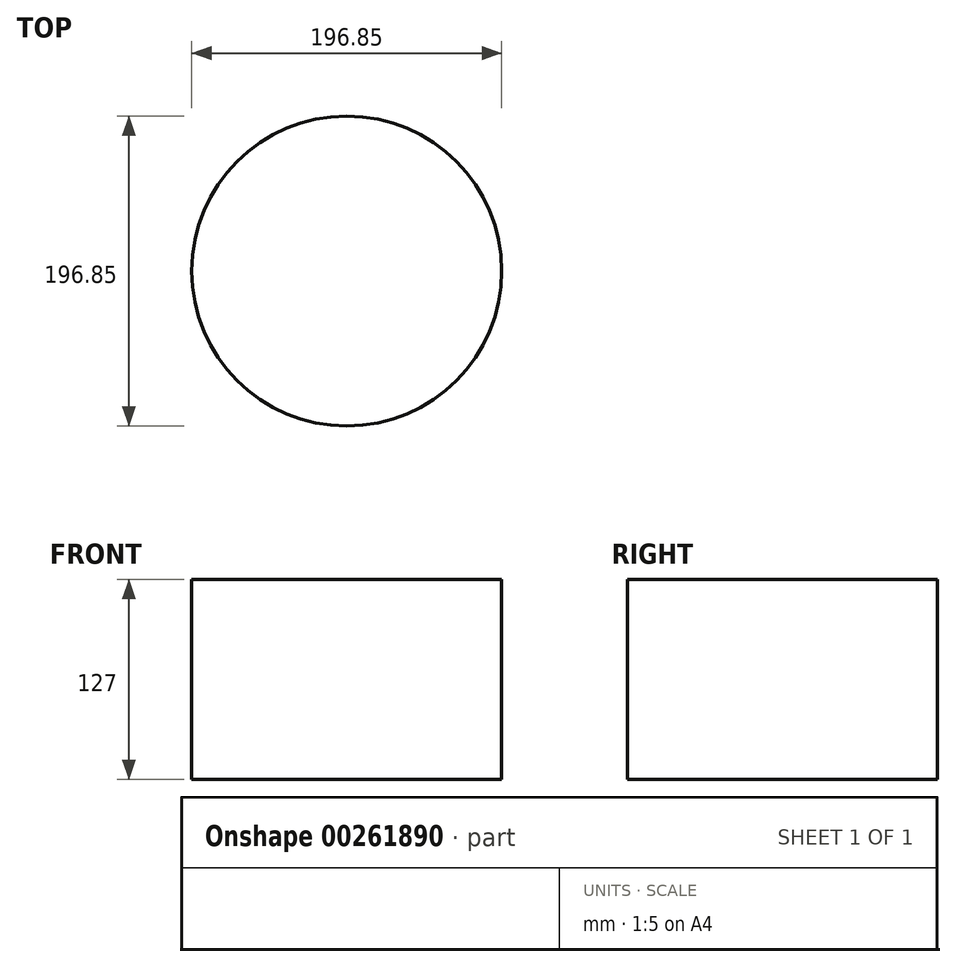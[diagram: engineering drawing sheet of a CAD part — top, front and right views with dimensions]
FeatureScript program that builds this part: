
annotation { "Feature Type Name" : "Feature", "Feature Type Description" : "" }
export const myFeature = defineFeature(function(context is Context, id is Id, definition is map)
    precondition{}
    {
        {
            var Q0;
            Q0=qCreatedBy(makeId("Top.planeOp"),FACE);
            var sketch = newSketch(context, id + "F0", { "sketchPlane" : qUnion([Q0])});
            skCircle(sketch, "E0", {"center": v(181.2, 194.06) * mm, "radius": 98.43 * mm});
            skFitSpline(sketch, "E1", {"points": [v(112.38, 300.15) * mm, v(105.16, 308.16) * mm, v(82.95, 328.17) * mm, v(51.55, 336.98) * mm, v(30.5, 338.33) * mm, v(28.58, 338.42) * mm]});
            skArc(sketch, "E2", {"start": v(112.38, 300.15) * mm, "mid": v(99.39, 290.49) * mm, "end": v(87.74, 279.25) * mm});
            skFitSpline(sketch, "E3", {"points": [v(-21.73, 290.15) * mm, v(-19.26, 290.89) * mm, v(-6.7, 294.37) * mm, v(16.72, 298.16) * mm, v(50.6, 296.23) * mm, v(74.98, 286.06) * mm, v(85.79, 280.32) * mm, v(87.74, 279.25) * mm]});
            skFitSpline(sketch, "E4", {"points": [v(28.58, 338.42) * mm, v(15.27, 329.22) * mm, v(-2.43, 313.76) * mm, v(-17.4, 295.85) * mm, v(-21.73, 290.15) * mm]});
            skFitSpline(sketch, "E5", {"points": [v(169.85, 320) * mm, v(168, 326.25) * mm, v(161.05, 343.52) * mm, v(145.87, 361.7) * mm, v(132.45, 371.54) * mm, v(128.53, 374.05) * mm]});
            skArc(sketch, "E6", {"start": v(169.85, 320) * mm, "mid": v(152.5, 317.21) * mm, "end": v(135.7, 312.04) * mm});
            skFitSpline(sketch, "E7", {"points": [v(64.83, 358.5) * mm, v(75.9, 355.55) * mm, v(95.15, 348.03) * mm, v(119.13, 330.35) * mm, v(130.66, 318.08) * mm, v(135.7, 312.04) * mm]});
            skFitSpline(sketch, "E8", {"points": [v(128.53, 374.05) * mm, v(114.46, 373.06) * mm, v(92.74, 369.09) * mm, v(72.05, 361.6) * mm, v(64.83, 358.5) * mm]});
            skFitSpline(sketch, "E9", {"points": [v(221.77, 313.82) * mm, v(221.62, 319.84) * mm, v(220.13, 336.34) * mm, v(214.41, 352.08) * mm, v(209.5, 361.5) * mm]});
            skArc(sketch, "E10", {"start": v(221.77, 313.82) * mm, "mid": v(209.13, 317.39) * mm, "end": v(196.19, 319.62) * mm});
            skFitSpline(sketch, "E11", {"points": [v(168.92, 372.54) * mm, v(176.73, 363.69) * mm, v(188.12, 346.58) * mm, v(194.4, 327.52) * mm, v(196.19, 319.62) * mm]});
            skFitSpline(sketch, "E12", {"points": [v(209.5, 361.5) * mm, v(203.15, 364.1) * mm, v(189.81, 368.61) * mm, v(176.04, 371.5) * mm, v(168.92, 372.54) * mm]});
            skFitSpline(sketch, "E13", {"points": [v(268.56, 285.47) * mm, v(270.9, 296.3) * mm, v(271.18, 307.75) * mm, v(270.11, 319.1) * mm]});
            skArc(sketch, "E14", {"start": v(268.56, 285.47) * mm, "mid": v(258.23, 294.33) * mm, "end": v(247.01, 302.03) * mm});
            skFitSpline(sketch, "E15", {"points": [v(243.53, 342.87) * mm, v(243.99, 340.98) * mm, v(246.06, 331.54) * mm, v(247.33, 317.47) * mm, v(247.2, 306.16) * mm, v(247.01, 302.03) * mm]});
            skFitSpline(sketch, "E16", {"points": [v(270.11, 319.1) * mm, v(262.18, 327.99) * mm, v(253.23, 335.96) * mm, v(243.53, 342.87) * mm]});
            skFitSpline(sketch, "E17", {"points": [v(298.96, 240.12) * mm, v(299.95, 241.56) * mm, v(302.07, 244.88) * mm, v(303.92, 248.35) * mm, v(304.86, 250.33) * mm]});
            skArc(sketch, "E18", {"start": v(298.96, 240.12) * mm, "mid": v(293.88, 251.42) * mm, "end": v(287.73, 262.17) * mm});
            skFitSpline(sketch, "E19", {"points": [v(294.02, 283.21) * mm, v(293.16, 278.62) * mm, v(291.38, 271.55) * mm, v(288.74, 264.58) * mm, v(287.73, 262.17) * mm]});
            skFitSpline(sketch, "E20", {"points": [v(304.86, 250.33) * mm, v(303.61, 256.7) * mm, v(300.57, 267.92) * mm, v(296.2, 278.62) * mm, v(294.02, 283.21) * mm]});
            skArc(sketch, "E21", {"start": v(72.43, 258.57) * mm, "mid": v(64.4, 242.56) * mm, "end": v(58.73, 225.58) * mm});
            skFitSpline(sketch, "E22", {"points": [v(-67.45, 179.6) * mm, v(-63.46, 183.22) * mm, v(-51.3, 193.48) * mm, v(-30.42, 208.94) * mm, v(3.18, 223.57) * mm, v(34.86, 226.39) * mm, v(52.01, 225.81) * mm, v(58.73, 225.58) * mm]});
            skFitSpline(sketch, "E23", {"points": [v(-44.97, 252.44) * mm, v(-50.68, 240.84) * mm, v(-60.08, 217) * mm, v(-65.64, 192.05) * mm, v(-67.45, 179.6) * mm]});
            skFitSpline(sketch, "E24", {"points": [v(72.43, 258.57) * mm, v(66.97, 261.58) * mm, v(53.74, 268.09) * mm, v(27.25, 273.24) * mm, v(-7.81, 269.43) * mm, v(-32.36, 259.91) * mm, v(-44.97, 252.44) * mm]});
            skArc(sketch, "E25", {"start": v(127.78, 79.44) * mm, "mid": v(134.38, 76.59) * mm, "end": v(141.13, 74.12) * mm});
            skFitSpline(sketch, "E26", {"points": [v(163.05, 64.87) * mm, v(155.49, 67.3) * mm, v(148.13, 70.39) * mm, v(141.13, 74.12) * mm]});
            skFitSpline(sketch, "E27", {"points": [v(192.18, -106.53) * mm, v(191, -104.48) * mm, v(185.24, -94.27) * mm, v(177.78, -80.03) * mm, v(170.5, -60.64) * mm, v(166.24, -44.44) * mm, v(163.7, -26.89) * mm, v(162.03, -12.95) * mm, v(160.61, -0.32) * mm, v(159.56, 11.2) * mm, v(158.96, 20.4) * mm, v(158.65, 27.67) * mm, v(158.5, 33.26) * mm, v(158.4, 38.54) * mm, v(158.47, 44.56) * mm, v(158.82, 50.13) * mm, v(159.9, 57.28) * mm, v(161.96, 62.59) * mm, v(163.05, 64.87) * mm]});
            skLineSegment(sketch, "E28", {"start": v(192.18, -106.53) * mm, "end": v(204.18, -127.4) * mm});
            skFitSpline(sketch, "E29", {"points": [v(204.18, -127.4) * mm, v(175.5, -124.78) * mm, v(146.5, -118.24) * mm, v(118.74, -108.24) * mm]});
            skLineSegment(sketch, "E30", {"start": v(118.74, -108.24) * mm, "end": v(112.6, -80.75) * mm});
            skFitSpline(sketch, "E31", {"points": [v(127.78, 79.44) * mm, v(127.77, 67.69) * mm, v(123, 44.73) * mm, v(113.63, 8.84) * mm, v(107.7, -33) * mm, v(108.94, -64.3) * mm, v(112.6, -80.75) * mm]});
            skArc(sketch, "E32", {"start": v(91.7, 104.7) * mm, "mid": v(96.9, 99.8) * mm, "end": v(102.34, 95.2) * mm});
            skLineSegment(sketch, "E33", {"start": v(102.34, 81.44) * mm, "end": v(102.34, 95.2) * mm});
            skFitSpline(sketch, "E34", {"points": [v(85.04, -70.15) * mm, v(84.92, -69.25) * mm, v(83.66, -58.77) * mm, v(83, -39.1) * mm, v(84.97, -11.88) * mm, v(89.3, 14.72) * mm, v(95.38, 39.88) * mm, v(100.17, 59.21) * mm, v(102.2, 72.62) * mm, v(102.44, 78.42) * mm, v(102.34, 81.44) * mm]});
            skLineSegment(sketch, "E35", {"start": v(85.04, -70.15) * mm, "end": v(85.04, -94.1) * mm});
            skFitSpline(sketch, "E36", {"points": [v(85.04, -94.1) * mm, v(65.63, -84.74) * mm, v(47.22, -73.63) * mm, v(30.4, -60.94) * mm]});
            skLineSegment(sketch, "E37", {"start": v(30.4, -60.94) * mm, "end": v(30.4, -46.88) * mm});
            skFitSpline(sketch, "E38", {"points": [v(91.7, 104.7) * mm, v(80.75, 90.5) * mm, v(57.76, 63.9) * mm, v(32, 15.88) * mm, v(30.72, -22.61) * mm, v(30.43, -43.72) * mm, v(30.4, -46.88) * mm]});
            skArc(sketch, "E39", {"start": v(63.68, 147.35) * mm, "mid": v(68.9, 135.9) * mm, "end": v(75.25, 125.02) * mm});
            skFitSpline(sketch, "E40", {"points": [v(5.2, -31.48) * mm, v(5.26, -29.47) * mm, v(5.6, -18.21) * mm, v(6.73, 3.38) * mm, v(17.08, 45.25) * mm, v(39.2, 79.68) * mm, v(61.28, 107.16) * mm, v(70.89, 119.18) * mm, v(75.25, 125.02) * mm]});
            skLineSegment(sketch, "E41", {"start": v(5.2, -31.48) * mm, "end": v(5.2, -39.56) * mm});
            skFitSpline(sketch, "E42", {"points": [v(5.2, -39.56) * mm, v(-19.44, -15.99) * mm, v(-36.1, 12.63) * mm]});
            skFitSpline(sketch, "E43", {"points": [v(-40.85, 20.8) * mm, v(-39.32, 17.99) * mm, v(-37.73, 15.26) * mm, v(-36.1, 12.63) * mm]});
            skFitSpline(sketch, "E44", {"points": [v(-44.98, 29.42) * mm, v(-42.99, 25.08) * mm, v(-40.85, 20.8) * mm]});
            skLineSegment(sketch, "E45", {"start": v(-45, 29.45) * mm, "end": v(-44.98, 29.42) * mm});
            skFitSpline(sketch, "E46", {"points": [v(63.68, 147.35) * mm, v(53.74, 142.94) * mm, v(31.68, 133.74) * mm, v(4.8, 111.7) * mm, v(-25.69, 79.28) * mm, v(-40.01, 49.87) * mm, v(-45, 29.45) * mm]});
            skLineSegment(sketch, "E47", {"start": v(356.15, -215.44) * mm, "end": v(347.48, -207.6) * mm});
            skFitSpline(sketch, "E48", {"points": [v(356.15, -215.44) * mm, v(360.28, -218.64) * mm, v(371.08, -225.9) * mm, v(390.9, -228.31) * mm, v(396.5, -219.74) * mm, v(397.75, -217.47) * mm]});
            skLineSegment(sketch, "E49", {"start": v(401.15, -209.22) * mm, "end": v(397.75, -217.47) * mm});
            skLineSegment(sketch, "E50", {"start": v(404.33, -198.93) * mm, "end": v(401.15, -209.22) * mm});
            skLineSegment(sketch, "E51", {"start": v(406.9, -187.4) * mm, "end": v(404.33, -198.93) * mm});
            skLineSegment(sketch, "E52", {"start": v(408.6, -175.72) * mm, "end": v(406.9, -187.4) * mm});
            skLineSegment(sketch, "E53", {"start": v(409.49, -164.74) * mm, "end": v(408.6, -175.72) * mm});
            skLineSegment(sketch, "E54", {"start": v(409.82, -154.97) * mm, "end": v(409.49, -164.74) * mm});
            skLineSegment(sketch, "E55", {"start": v(409.82, -146.3) * mm, "end": v(409.82, -154.97) * mm});
            skLineSegment(sketch, "E56", {"start": v(409.84, -138.33) * mm, "end": v(409.82, -146.3) * mm});
            skLineSegment(sketch, "E57", {"start": v(410.15, -130.6) * mm, "end": v(409.84, -138.33) * mm});
            skLineSegment(sketch, "E58", {"start": v(411.14, -123.04) * mm, "end": v(410.15, -130.6) * mm});
            skLineSegment(sketch, "E59", {"start": v(413.27, -115.98) * mm, "end": v(411.14, -123.04) * mm});
            skLineSegment(sketch, "E60", {"start": v(416.85, -110.06) * mm, "end": v(413.27, -115.98) * mm});
            skLineSegment(sketch, "E61", {"start": v(421.96, -106) * mm, "end": v(416.85, -110.06) * mm});
            skLineSegment(sketch, "E62", {"start": v(428.28, -104.27) * mm, "end": v(421.96, -106) * mm});
            skLineSegment(sketch, "E63", {"start": v(435.24, -104.85) * mm, "end": v(428.28, -104.27) * mm});
            skLineSegment(sketch, "E64", {"start": v(442.28, -107.26) * mm, "end": v(435.24, -104.85) * mm});
            skLineSegment(sketch, "E65", {"start": v(449.03, -110.8) * mm, "end": v(442.28, -107.26) * mm});
            skLineSegment(sketch, "E66", {"start": v(455.56, -114.94) * mm, "end": v(449.03, -110.8) * mm});
            skLineSegment(sketch, "E67", {"start": v(469.4, -124.38) * mm, "end": v(455.56, -114.94) * mm});
            skLineSegment(sketch, "E68", {"start": v(477.76, -129.7) * mm, "end": v(469.4, -124.38) * mm});
            skLineSegment(sketch, "E69", {"start": v(487.39, -135.15) * mm, "end": v(477.76, -129.7) * mm});
            skLineSegment(sketch, "E70", {"start": v(497.98, -140.3) * mm, "end": v(487.39, -135.15) * mm});
            skLineSegment(sketch, "E71", {"start": v(508.77, -144.65) * mm, "end": v(497.98, -140.3) * mm});
            skLineSegment(sketch, "E72", {"start": v(518.83, -147.8) * mm, "end": v(508.77, -144.65) * mm});
            skLineSegment(sketch, "E73", {"start": v(527.34, -149.63) * mm, "end": v(518.83, -147.8) * mm});
            skLineSegment(sketch, "E74", {"start": v(533.97, -150.24) * mm, "end": v(527.34, -149.63) * mm});
            skLineSegment(sketch, "E75", {"start": v(538.8, -149.86) * mm, "end": v(533.97, -150.24) * mm});
            skLineSegment(sketch, "E76", {"start": v(542.23, -148.67) * mm, "end": v(538.8, -149.86) * mm});
            skLineSegment(sketch, "E77", {"start": v(544.77, -146.66) * mm, "end": v(542.23, -148.67) * mm});
            skLineSegment(sketch, "E78", {"start": v(546.75, -143.61) * mm, "end": v(544.77, -146.66) * mm});
            skLineSegment(sketch, "E79", {"start": v(548.27, -139.01) * mm, "end": v(546.75, -143.61) * mm});
            skLineSegment(sketch, "E80", {"start": v(549.26, -132.41) * mm, "end": v(548.27, -139.01) * mm});
            skLineSegment(sketch, "E81", {"start": v(549.57, -123.67) * mm, "end": v(549.26, -132.41) * mm});
            skLineSegment(sketch, "E82", {"start": v(548.9, -113.1) * mm, "end": v(549.57, -123.67) * mm});
            skLineSegment(sketch, "E83", {"start": v(547.3, -101.55) * mm, "end": v(548.9, -113.1) * mm});
            skLineSegment(sketch, "E84", {"start": v(544.84, -90.04) * mm, "end": v(547.3, -101.55) * mm});
            skLineSegment(sketch, "E85", {"start": v(541.87, -79.4) * mm, "end": v(544.84, -90.04) * mm});
            skLineSegment(sketch, "E86", {"start": v(538.75, -69.98) * mm, "end": v(541.87, -79.4) * mm});
            skLineSegment(sketch, "E87", {"start": v(532.98, -54.05) * mm, "end": v(538.75, -69.98) * mm});
            skLineSegment(sketch, "E88", {"start": v(530.6, -46.63) * mm, "end": v(532.98, -54.05) * mm});
            skLineSegment(sketch, "E89", {"start": v(528.9, -39.2) * mm, "end": v(530.6, -46.63) * mm});
            skLineSegment(sketch, "E90", {"start": v(528.36, -31.85) * mm, "end": v(528.9, -39.2) * mm});
            skLineSegment(sketch, "E91", {"start": v(529.55, -25.1) * mm, "end": v(528.36, -31.85) * mm});
            skLineSegment(sketch, "E92", {"start": v(532.78, -19.5) * mm, "end": v(529.55, -25.1) * mm});
            skLineSegment(sketch, "E93", {"start": v(537.93, -15.62) * mm, "end": v(532.78, -19.5) * mm});
            skLineSegment(sketch, "E94", {"start": v(544.51, -13.67) * mm, "end": v(537.93, -15.62) * mm});
            skLineSegment(sketch, "E95", {"start": v(551.85, -13.36) * mm, "end": v(544.51, -13.67) * mm});
            skLineSegment(sketch, "E96", {"start": v(559.42, -14.25) * mm, "end": v(551.85, -13.36) * mm});
            skLineSegment(sketch, "E97", {"start": v(567.02, -15.85) * mm, "end": v(559.42, -14.25) * mm});
            skLineSegment(sketch, "E98", {"start": v(574.84, -17.8) * mm, "end": v(567.02, -15.85) * mm});
            skLineSegment(sketch, "E99", {"start": v(583.35, -19.96) * mm, "end": v(574.84, -17.8) * mm});
            skLineSegment(sketch, "E100", {"start": v(592.98, -22.12) * mm, "end": v(583.35, -19.96) * mm});
            skLineSegment(sketch, "E101", {"start": v(603.8, -24.03) * mm, "end": v(592.98, -22.12) * mm});
            skLineSegment(sketch, "E102", {"start": v(615.43, -25.37) * mm, "end": v(603.8, -24.03) * mm});
            skLineSegment(sketch, "E103", {"start": v(627.01, -25.93) * mm, "end": v(615.43, -25.37) * mm});
            skLineSegment(sketch, "E104", {"start": v(637.55, -25.63) * mm, "end": v(627.01, -25.93) * mm});
            skLineSegment(sketch, "E105", {"start": v(646.32, -24.59) * mm, "end": v(637.55, -25.63) * mm});
            skLineSegment(sketch, "E106", {"start": v(652.92, -22.99) * mm, "end": v(646.32, -24.59) * mm});
            skLineSegment(sketch, "E107", {"start": v(657.54, -21) * mm, "end": v(652.92, -22.99) * mm});
            skLineSegment(sketch, "E108", {"start": v(660.54, -18.72) * mm, "end": v(657.54, -21) * mm});
            skLineSegment(sketch, "E109", {"start": v(662.4, -15.95) * mm, "end": v(660.54, -18.72) * mm});
            skLineSegment(sketch, "E110", {"start": v(663.28, -12.4) * mm, "end": v(662.4, -15.95) * mm});
            skLineSegment(sketch, "E111", {"start": v(663.26, -7.6) * mm, "end": v(663.28, -12.4) * mm});
            skLineSegment(sketch, "E112", {"start": v(662.06, -1.14) * mm, "end": v(663.26, -7.6) * mm});
            skLineSegment(sketch, "E113", {"start": v(659.47, 7.04) * mm, "end": v(662.06, -1.14) * mm});
            skLineSegment(sketch, "E114", {"start": v(655.43, 16.64) * mm, "end": v(659.47, 7.04) * mm});
            skLineSegment(sketch, "E115", {"start": v(650.15, 26.87) * mm, "end": v(655.43, 16.64) * mm});
            skLineSegment(sketch, "E116", {"start": v(644.06, 36.88) * mm, "end": v(650.15, 26.87) * mm});
            skLineSegment(sketch, "E117", {"start": v(637.76, 46.02) * mm, "end": v(644.06, 36.88) * mm});
            skLineSegment(sketch, "E118", {"start": v(631.66, 54) * mm, "end": v(637.76, 46.02) * mm});
            skLineSegment(sketch, "E119", {"start": v(620.86, 67.39) * mm, "end": v(631.66, 54) * mm});
            skLineSegment(sketch, "E120", {"start": v(616.14, 73.69) * mm, "end": v(620.86, 67.39) * mm});
            skLineSegment(sketch, "E121", {"start": v(612.08, 80.16) * mm, "end": v(616.14, 73.69) * mm});
            skLineSegment(sketch, "E122", {"start": v(609.13, 86.9) * mm, "end": v(612.08, 80.16) * mm});
            skLineSegment(sketch, "E123", {"start": v(607.94, 93.62) * mm, "end": v(609.13, 86.9) * mm});
            skLineSegment(sketch, "E124", {"start": v(609, 99.92) * mm, "end": v(607.94, 93.62) * mm});
            skLineSegment(sketch, "E125", {"start": v(612.38, 105.28) * mm, "end": v(609, 99.92) * mm});
            skLineSegment(sketch, "E126", {"start": v(617.8, 109.35) * mm, "end": v(612.38, 105.28) * mm});
            skLineSegment(sketch, "E127", {"start": v(624.52, 112.12) * mm, "end": v(617.8, 109.35) * mm});
            skLineSegment(sketch, "E128", {"start": v(631.94, 113.82) * mm, "end": v(624.52, 112.12) * mm});
            skLineSegment(sketch, "E129", {"start": v(639.66, 114.83) * mm, "end": v(631.94, 113.82) * mm});
            skLineSegment(sketch, "E130", {"start": v(647.76, 115.57) * mm, "end": v(639.66, 114.83) * mm});
            skLineSegment(sketch, "E131", {"start": v(656.53, 116.3) * mm, "end": v(647.76, 115.57) * mm});
            skLineSegment(sketch, "E132", {"start": v(666.3, 117.35) * mm, "end": v(656.53, 116.3) * mm});
            skLineSegment(sketch, "E133", {"start": v(677.1, 118.95) * mm, "end": v(666.3, 117.35) * mm});
            skLineSegment(sketch, "E134", {"start": v(688.45, 121.31) * mm, "end": v(677.1, 118.95) * mm});
            skLineSegment(sketch, "E135", {"start": v(699.58, 124.36) * mm, "end": v(688.45, 121.31) * mm});
            skLineSegment(sketch, "E136", {"start": v(709.56, 127.94) * mm, "end": v(699.58, 124.36) * mm});
            skLineSegment(sketch, "E137", {"start": v(717.66, 131.65) * mm, "end": v(709.56, 127.94) * mm});
            skLineSegment(sketch, "E138", {"start": v(723.6, 135.28) * mm, "end": v(717.66, 131.65) * mm});
            skLineSegment(sketch, "E139", {"start": v(727.54, 138.66) * mm, "end": v(723.6, 135.28) * mm});
            skLineSegment(sketch, "E140", {"start": v(729.8, 141.83) * mm, "end": v(727.54, 138.66) * mm});
            skLineSegment(sketch, "E141", {"start": v(730.77, 145.11) * mm, "end": v(729.8, 141.83) * mm});
            skLineSegment(sketch, "E142", {"start": v(730.6, 148.8) * mm, "end": v(730.77, 145.11) * mm});
            skLineSegment(sketch, "E143", {"start": v(729.1, 153.34) * mm, "end": v(730.6, 148.8) * mm});
            skLineSegment(sketch, "E144", {"start": v(726.02, 159) * mm, "end": v(729.1, 153.34) * mm});
            skLineSegment(sketch, "E145", {"start": v(721.1, 165.84) * mm, "end": v(726.02, 159) * mm});
            skLineSegment(sketch, "E146", {"start": v(714.36, 173.53) * mm, "end": v(721.1, 165.84) * mm});
            skLineSegment(sketch, "E147", {"start": v(706.23, 181.5) * mm, "end": v(714.36, 173.53) * mm});
            skLineSegment(sketch, "E148", {"start": v(697.37, 189.1) * mm, "end": v(706.23, 181.5) * mm});
            skLineSegment(sketch, "E149", {"start": v(688.48, 195.83) * mm, "end": v(697.37, 189.1) * mm});
            skLineSegment(sketch, "E150", {"start": v(680.15, 201.63) * mm, "end": v(688.48, 195.83) * mm});
            skLineSegment(sketch, "E151", {"start": v(665.54, 211.18) * mm, "end": v(680.15, 201.63) * mm});
            skLineSegment(sketch, "E152", {"start": v(659.04, 215.72) * mm, "end": v(665.54, 211.18) * mm});
            skLineSegment(sketch, "E153", {"start": v(653.15, 220.62) * mm, "end": v(659.04, 215.72) * mm});
            skLineSegment(sketch, "E154", {"start": v(648.22, 226.06) * mm, "end": v(653.15, 220.62) * mm});
            skLineSegment(sketch, "E155", {"start": v(644.9, 232.03) * mm, "end": v(648.22, 226.06) * mm});
            skLineSegment(sketch, "E156", {"start": v(643.8, 238.25) * mm, "end": v(644.9, 232.03) * mm});
            skLineSegment(sketch, "E157", {"start": v(645.2, 244.35) * mm, "end": v(643.8, 238.25) * mm});
            skLineSegment(sketch, "E158", {"start": v(648.88, 249.89) * mm, "end": v(645.2, 244.35) * mm});
            skLineSegment(sketch, "E159", {"start": v(654.3, 254.63) * mm, "end": v(648.88, 249.89) * mm});
            skLineSegment(sketch, "E160", {"start": v(660.74, 258.62) * mm, "end": v(654.3, 254.63) * mm});
            skLineSegment(sketch, "E161", {"start": v(667.78, 262.05) * mm, "end": v(660.74, 258.62) * mm});
            skLineSegment(sketch, "E162", {"start": v(675.27, 265.28) * mm, "end": v(667.78, 262.05) * mm});
            skLineSegment(sketch, "E163", {"start": v(683.4, 268.68) * mm, "end": v(675.27, 265.28) * mm});
            skLineSegment(sketch, "E164", {"start": v(692.37, 272.64) * mm, "end": v(683.4, 268.68) * mm});
            skLineSegment(sketch, "E165", {"start": v(702.12, 277.4) * mm, "end": v(692.37, 272.64) * mm});
            skLineSegment(sketch, "E166", {"start": v(712.2, 283) * mm, "end": v(702.12, 277.4) * mm});
            skLineSegment(sketch, "E167", {"start": v(721.88, 289.2) * mm, "end": v(712.2, 283) * mm});
            skLineSegment(sketch, "E168", {"start": v(730.39, 295.55) * mm, "end": v(721.88, 289.2) * mm});
            skLineSegment(sketch, "E169", {"start": v(737.12, 301.55) * mm, "end": v(730.39, 295.55) * mm});
            skLineSegment(sketch, "E170", {"start": v(741.87, 306.83) * mm, "end": v(737.12, 301.55) * mm});
            skLineSegment(sketch, "E171", {"start": v(744.77, 311.33) * mm, "end": v(741.87, 306.83) * mm});
            skLineSegment(sketch, "E172", {"start": v(746.09, 315.14) * mm, "end": v(744.77, 311.33) * mm});
            skLineSegment(sketch, "E173", {"start": v(746.11, 318.64) * mm, "end": v(746.09, 315.14) * mm});
            skLineSegment(sketch, "E174", {"start": v(744.9, 322.15) * mm, "end": v(746.11, 318.64) * mm});
            skLineSegment(sketch, "E175", {"start": v(742.18, 326.03) * mm, "end": v(744.9, 322.15) * mm});
            skLineSegment(sketch, "E176", {"start": v(737.63, 330.45) * mm, "end": v(742.18, 326.03) * mm});
            skLineSegment(sketch, "E177", {"start": v(731.02, 335.43) * mm, "end": v(737.63, 330.45) * mm});
            skLineSegment(sketch, "E178", {"start": v(722.46, 340.7) * mm, "end": v(731.02, 335.43) * mm});
            skLineSegment(sketch, "E179", {"start": v(712.43, 345.85) * mm, "end": v(722.46, 340.7) * mm});
            skLineSegment(sketch, "E180", {"start": v(701.76, 350.44) * mm, "end": v(712.43, 345.85) * mm});
            skLineSegment(sketch, "E181", {"start": v(691.27, 354.28) * mm, "end": v(701.76, 350.44) * mm});
            skLineSegment(sketch, "E182", {"start": v(681.5, 357.38) * mm, "end": v(691.27, 354.28) * mm});
            skLineSegment(sketch, "E183", {"start": v(672.63, 359.97) * mm, "end": v(681.5, 357.38) * mm});
            skLineSegment(sketch, "E184", {"start": v(664.5, 362.3) * mm, "end": v(672.63, 359.97) * mm});
            skLineSegment(sketch, "E185", {"start": v(656.88, 364.77) * mm, "end": v(664.5, 362.3) * mm});
            skLineSegment(sketch, "E186", {"start": v(649.77, 367.7) * mm, "end": v(656.88, 364.77) * mm});
            skLineSegment(sketch, "E187", {"start": v(643.42, 371.37) * mm, "end": v(649.77, 367.7) * mm});
            skLineSegment(sketch, "E188", {"start": v(638.44, 376.02) * mm, "end": v(643.42, 371.37) * mm});
            skLineSegment(sketch, "E189", {"start": v(635.44, 381.56) * mm, "end": v(638.44, 376.02) * mm});
            skLineSegment(sketch, "E190", {"start": v(634.8, 387.68) * mm, "end": v(635.44, 381.56) * mm});
            skLineSegment(sketch, "E191", {"start": v(636.54, 394) * mm, "end": v(634.8, 387.68) * mm});
            skLineSegment(sketch, "E192", {"start": v(640.17, 400.13) * mm, "end": v(636.54, 394) * mm});
            skLineSegment(sketch, "E193", {"start": v(645.07, 405.87) * mm, "end": v(640.17, 400.13) * mm});
            skLineSegment(sketch, "E194", {"start": v(650.76, 411.28) * mm, "end": v(645.07, 405.87) * mm});
            skLineSegment(sketch, "E195", {"start": v(656.98, 416.61) * mm, "end": v(650.76, 411.28) * mm});
            skLineSegment(sketch, "E196", {"start": v(663.77, 422.25) * mm, "end": v(656.98, 416.61) * mm});
            skLineSegment(sketch, "E197", {"start": v(671.18, 428.63) * mm, "end": v(663.77, 422.25) * mm});
            skLineSegment(sketch, "E198", {"start": v(679.1, 435.94) * mm, "end": v(671.18, 428.63) * mm});
            skLineSegment(sketch, "E199", {"start": v(687.13, 444.12) * mm, "end": v(679.1, 435.94) * mm});
            skLineSegment(sketch, "E200", {"start": v(694.65, 452.75) * mm, "end": v(687.13, 444.12) * mm});
            skLineSegment(sketch, "E201", {"start": v(701.08, 461.26) * mm, "end": v(694.65, 452.75) * mm});
            skLineSegment(sketch, "E202", {"start": v(705.93, 468.96) * mm, "end": v(701.08, 461.26) * mm});
            skLineSegment(sketch, "E203", {"start": v(709.1, 475.49) * mm, "end": v(705.93, 468.96) * mm});
            skLineSegment(sketch, "E204", {"start": v(710.7, 480.72) * mm, "end": v(709.1, 475.49) * mm});
            skLineSegment(sketch, "E205", {"start": v(710.96, 484.91) * mm, "end": v(710.7, 480.72) * mm});
            skLineSegment(sketch, "E206", {"start": v(710.07, 488.34) * mm, "end": v(710.96, 484.91) * mm});
            skLineSegment(sketch, "E207", {"start": v(707.94, 491.44) * mm, "end": v(710.07, 488.34) * mm});
            skLineSegment(sketch, "E208", {"start": v(704.3, 494.39) * mm, "end": v(707.94, 491.44) * mm});
            skLineSegment(sketch, "E209", {"start": v(698.8, 497.33) * mm, "end": v(704.3, 494.39) * mm});
            skLineSegment(sketch, "E210", {"start": v(691.17, 500.2) * mm, "end": v(698.8, 497.33) * mm});
            skLineSegment(sketch, "E211", {"start": v(681.62, 502.8) * mm, "end": v(691.17, 500.2) * mm});
            skLineSegment(sketch, "E212", {"start": v(670.67, 504.85) * mm, "end": v(681.62, 502.8) * mm});
            skLineSegment(sketch, "E213", {"start": v(659.2, 506.25) * mm, "end": v(670.67, 504.85) * mm});
            skLineSegment(sketch, "E214", {"start": v(648.02, 506.98) * mm, "end": v(659.2, 506.25) * mm});
            skLineSegment(sketch, "E215", {"start": v(637.68, 507.24) * mm, "end": v(648.02, 506.98) * mm});
            skLineSegment(sketch, "E216", {"start": v(619.75, 507.21) * mm, "end": v(637.68, 507.24) * mm});
            skLineSegment(sketch, "E217", {"start": v(611.7, 507.44) * mm, "end": v(619.75, 507.21) * mm});
            skLineSegment(sketch, "E218", {"start": v(604, 508.23) * mm, "end": v(611.7, 507.44) * mm});
            skLineSegment(sketch, "E219", {"start": v(596.84, 509.93) * mm, "end": v(604, 508.23) * mm});
            skLineSegment(sketch, "E220", {"start": v(590.72, 512.88) * mm, "end": v(596.84, 509.93) * mm});
            skLineSegment(sketch, "E221", {"start": v(586.2, 517.22) * mm, "end": v(590.72, 512.88) * mm});
            skLineSegment(sketch, "E222", {"start": v(583.76, 522.8) * mm, "end": v(586.2, 517.22) * mm});
            skLineSegment(sketch, "E223", {"start": v(583.48, 529.26) * mm, "end": v(583.76, 522.8) * mm});
            skLineSegment(sketch, "E224", {"start": v(585.1, 536.1) * mm, "end": v(583.48, 529.26) * mm});
            skLineSegment(sketch, "E225", {"start": v(588.12, 543) * mm, "end": v(585.1, 536.1) * mm});
            skLineSegment(sketch, "E226", {"start": v(592.04, 549.8) * mm, "end": v(588.12, 543) * mm});
            skLineSegment(sketch, "E227", {"start": v(596.5, 556.72) * mm, "end": v(592.04, 549.8) * mm});
            skLineSegment(sketch, "E228", {"start": v(601.43, 564.03) * mm, "end": v(596.5, 556.72) * mm});
            skLineSegment(sketch, "E229", {"start": v(606.77, 572.19) * mm, "end": v(601.43, 564.03) * mm});
            skLineSegment(sketch, "E230", {"start": v(612.36, 581.33) * mm, "end": v(606.77, 572.19) * mm});
            skLineSegment(sketch, "E231", {"start": v(617.84, 591.31) * mm, "end": v(612.36, 581.33) * mm});
            skLineSegment(sketch, "E232", {"start": v(622.74, 601.65) * mm, "end": v(617.84, 591.31) * mm});
            skLineSegment(sketch, "E233", {"start": v(626.66, 611.58) * mm, "end": v(622.74, 601.65) * mm});
            skLineSegment(sketch, "E234", {"start": v(629.35, 620.4) * mm, "end": v(626.66, 611.58) * mm});
            skLineSegment(sketch, "E235", {"start": v(630.72, 627.63) * mm, "end": v(629.35, 620.4) * mm});
            skLineSegment(sketch, "E236", {"start": v(630.9, 633.27) * mm, "end": v(630.72, 627.63) * mm});
            skLineSegment(sketch, "E237", {"start": v(630.09, 637.49) * mm, "end": v(630.9, 633.27) * mm});
            skLineSegment(sketch, "E238", {"start": v(628.3, 640.66) * mm, "end": v(630.09, 637.49) * mm});
            skLineSegment(sketch, "E239", {"start": v(625.46, 643.13) * mm, "end": v(628.3, 640.66) * mm});
            skLineSegment(sketch, "E240", {"start": v(621.22, 645.03) * mm, "end": v(625.46, 643.13) * mm});
            skLineSegment(sketch, "E241", {"start": v(615.2, 646.38) * mm, "end": v(621.22, 645.03) * mm});
            skLineSegment(sketch, "E242", {"start": v(607.25, 647.1) * mm, "end": v(615.2, 646.38) * mm});
            skLineSegment(sketch, "E243", {"start": v(597.5, 646.99) * mm, "end": v(607.25, 647.1) * mm});
            skLineSegment(sketch, "E244", {"start": v(586.52, 646.05) * mm, "end": v(597.5, 646.99) * mm});
            skLineSegment(sketch, "E245", {"start": v(575.14, 644.32) * mm, "end": v(586.52, 646.05) * mm});
            skLineSegment(sketch, "E246", {"start": v(564.15, 642.04) * mm, "end": v(575.14, 644.32) * mm});
            skLineSegment(sketch, "E247", {"start": v(554.06, 639.5) * mm, "end": v(564.15, 642.04) * mm});
            skLineSegment(sketch, "E248", {"start": v(536.59, 634.62) * mm, "end": v(554.06, 639.5) * mm});
            skLineSegment(sketch, "E249", {"start": v(528.69, 632.64) * mm, "end": v(536.59, 634.62) * mm});
            skLineSegment(sketch, "E250", {"start": v(521.02, 631.32) * mm, "end": v(528.69, 632.64) * mm});
            skLineSegment(sketch, "E251", {"start": v(513.68, 630.99) * mm, "end": v(521.02, 631.32) * mm});
            skLineSegment(sketch, "E252", {"start": v(506.97, 632.08) * mm, "end": v(513.68, 630.99) * mm});
            skLineSegment(sketch, "E253", {"start": v(501.4, 634.9) * mm, "end": v(506.97, 632.08) * mm});
            skLineSegment(sketch, "E254", {"start": v(497.47, 639.47) * mm, "end": v(501.4, 634.9) * mm});
            skLineSegment(sketch, "E255", {"start": v(495.36, 645.46) * mm, "end": v(497.47, 639.47) * mm});
            skLineSegment(sketch, "E256", {"start": v(494.98, 652.42) * mm, "end": v(495.36, 645.46) * mm});
            skLineSegment(sketch, "E257", {"start": v(495.95, 659.84) * mm, "end": v(494.98, 652.42) * mm});
            skLineSegment(sketch, "E258", {"start": v(497.83, 667.49) * mm, "end": v(495.95, 659.84) * mm});
            skLineSegment(sketch, "E259", {"start": v(500.27, 675.34) * mm, "end": v(497.83, 667.49) * mm});
            skLineSegment(sketch, "E260", {"start": v(503.06, 683.74) * mm, "end": v(500.27, 675.34) * mm});
            skLineSegment(sketch, "E261", {"start": v(506.03, 692.99) * mm, "end": v(503.06, 683.74) * mm});
            skLineSegment(sketch, "E262", {"start": v(509.03, 703.2) * mm, "end": v(506.03, 692.99) * mm});
            skLineSegment(sketch, "E263", {"start": v(511.7, 714.22) * mm, "end": v(509.03, 703.2) * mm});
            skLineSegment(sketch, "E264", {"start": v(513.8, 725.45) * mm, "end": v(511.7, 714.22) * mm});
            skLineSegment(sketch, "E265", {"start": v(515.05, 736.07) * mm, "end": v(513.8, 725.45) * mm});
            skLineSegment(sketch, "E266", {"start": v(515.4, 745.34) * mm, "end": v(515.05, 736.07) * mm});
            skLineSegment(sketch, "E267", {"start": v(514.92, 752.86) * mm, "end": v(515.4, 745.34) * mm});
            skLineSegment(sketch, "E268", {"start": v(513.68, 758.47) * mm, "end": v(514.92, 752.86) * mm});
            skLineSegment(sketch, "E269", {"start": v(511.8, 762.48) * mm, "end": v(513.68, 758.47) * mm});
            skLineSegment(sketch, "E270", {"start": v(509.28, 765.2) * mm, "end": v(511.8, 762.48) * mm});
            skLineSegment(sketch, "E271", {"start": v(505.9, 766.93) * mm, "end": v(509.28, 765.2) * mm});
            skLineSegment(sketch, "E272", {"start": v(501.36, 767.72) * mm, "end": v(505.9, 766.93) * mm});
            skLineSegment(sketch, "E273", {"start": v(495.29, 767.51) * mm, "end": v(501.36, 767.72) * mm});
            skLineSegment(sketch, "E274", {"start": v(487.57, 766.2) * mm, "end": v(495.29, 767.51) * mm});
            skLineSegment(sketch, "E275", {"start": v(478.3, 763.63) * mm, "end": v(487.57, 766.2) * mm});
            skLineSegment(sketch, "E276", {"start": v(468.06, 759.92) * mm, "end": v(478.3, 763.63) * mm});
            skLineSegment(sketch, "E277", {"start": v(457.57, 755.35) * mm, "end": v(468.06, 759.92) * mm});
            skLineSegment(sketch, "E278", {"start": v(447.5, 750.3) * mm, "end": v(457.57, 755.35) * mm});
            skLineSegment(sketch, "E279", {"start": v(438.32, 745.24) * mm, "end": v(447.5, 750.3) * mm});
            skLineSegment(sketch, "E280", {"start": v(422.5, 735.94) * mm, "end": v(438.32, 745.24) * mm});
            skLineSegment(sketch, "E281", {"start": v(415.3, 731.98) * mm, "end": v(422.5, 735.94) * mm});
            skLineSegment(sketch, "E282", {"start": v(408.22, 728.68) * mm, "end": v(415.3, 731.98) * mm});
            skLineSegment(sketch, "E283", {"start": v(401.2, 726.41) * mm, "end": v(408.22, 728.68) * mm});
            skLineSegment(sketch, "E284", {"start": v(394.45, 725.65) * mm, "end": v(401.2, 726.41) * mm});
            skLineSegment(sketch, "E285", {"start": v(388.33, 726.8) * mm, "end": v(394.45, 725.65) * mm});
            skLineSegment(sketch, "E286", {"start": v(383.32, 730.05) * mm, "end": v(388.33, 726.8) * mm});
            skLineSegment(sketch, "E287", {"start": v(379.67, 735.15) * mm, "end": v(383.32, 730.05) * mm});
            skLineSegment(sketch, "E288", {"start": v(377.43, 741.68) * mm, "end": v(379.67, 735.15) * mm});
            skLineSegment(sketch, "E289", {"start": v(376.39, 749.05) * mm, "end": v(377.43, 741.68) * mm});
            skLineSegment(sketch, "E290", {"start": v(376.19, 756.87) * mm, "end": v(376.39, 749.05) * mm});
            skLineSegment(sketch, "E291", {"start": v(376.5, 765.12) * mm, "end": v(376.19, 756.87) * mm});
            skLineSegment(sketch, "E292", {"start": v(377.58, 783.62) * mm, "end": v(376.5, 765.12) * mm});
            skLineSegment(sketch, "E293", {"start": v(377.89, 794.23) * mm, "end": v(377.58, 783.62) * mm});
            skLineSegment(sketch, "E294", {"start": v(377.76, 805.51) * mm, "end": v(377.89, 794.23) * mm});
            skLineSegment(sketch, "E295", {"start": v(377.02, 816.86) * mm, "end": v(377.76, 805.51) * mm});
            skLineSegment(sketch, "E296", {"start": v(375.65, 827.48) * mm, "end": v(377.02, 816.86) * mm});
            skLineSegment(sketch, "E297", {"start": v(373.72, 836.68) * mm, "end": v(375.65, 827.48) * mm});
            skLineSegment(sketch, "E298", {"start": v(371.39, 843.94) * mm, "end": v(373.72, 836.68) * mm});
            skLineSegment(sketch, "E299", {"start": v(368.8, 849.25) * mm, "end": v(371.39, 843.94) * mm});
            skLineSegment(sketch, "E300", {"start": v(365.98, 852.8) * mm, "end": v(368.8, 849.25) * mm});
            skLineSegment(sketch, "E301", {"start": v(362.85, 854.94) * mm, "end": v(365.98, 852.8) * mm});
            skLineSegment(sketch, "E302", {"start": v(359.14, 855.83) * mm, "end": v(362.85, 854.94) * mm});
            skLineSegment(sketch, "E303", {"start": v(354.57, 855.55) * mm, "end": v(359.14, 855.83) * mm});
            skLineSegment(sketch, "E304", {"start": v(348.83, 853.92) * mm, "end": v(354.57, 855.55) * mm});
            skLineSegment(sketch, "E305", {"start": v(341.77, 850.77) * mm, "end": v(348.83, 853.92) * mm});
            skLineSegment(sketch, "E306", {"start": v(333.57, 846.1) * mm, "end": v(341.77, 850.77) * mm});
            skLineSegment(sketch, "E307", {"start": v(324.65, 840.03) * mm, "end": v(333.57, 846.1) * mm});
            skLineSegment(sketch, "E308", {"start": v(315.63, 833.04) * mm, "end": v(324.65, 840.03) * mm});
            skLineSegment(sketch, "E309", {"start": v(307.12, 825.7) * mm, "end": v(315.63, 833.04) * mm});
            skLineSegment(sketch, "E310", {"start": v(299.4, 818.46) * mm, "end": v(307.12, 825.7) * mm});
            skLineSegment(sketch, "E311", {"start": v(286.22, 805.46) * mm, "end": v(299.4, 818.46) * mm});
            skLineSegment(sketch, "E312", {"start": v(280.17, 799.8) * mm, "end": v(286.22, 805.46) * mm});
            skLineSegment(sketch, "E313", {"start": v(274.1, 794.8) * mm, "end": v(280.17, 799.8) * mm});
            skLineSegment(sketch, "E314", {"start": v(267.86, 790.8) * mm, "end": v(274.1, 794.8) * mm});
            skLineSegment(sketch, "E315", {"start": v(261.53, 788.31) * mm, "end": v(267.86, 790.8) * mm});
            skLineSegment(sketch, "E316", {"start": v(255.33, 787.8) * mm, "end": v(261.53, 788.31) * mm});
            skLineSegment(sketch, "E317", {"start": v(249.67, 789.53) * mm, "end": v(255.33, 787.8) * mm});
            skLineSegment(sketch, "E318", {"start": v(244.84, 793.42) * mm, "end": v(249.67, 789.53) * mm});
            skLineSegment(sketch, "E319", {"start": v(241, 799.06) * mm, "end": v(244.84, 793.42) * mm});
            skLineSegment(sketch, "E320", {"start": v(238.14, 805.87) * mm, "end": v(241, 799.06) * mm});
            skLineSegment(sketch, "E321", {"start": v(235.95, 813.38) * mm, "end": v(238.14, 805.87) * mm});
            skLineSegment(sketch, "E322", {"start": v(234.2, 821.46) * mm, "end": v(235.95, 813.38) * mm});
            skLineSegment(sketch, "E323", {"start": v(230.72, 839.65) * mm, "end": v(234.2, 821.46) * mm});
            skLineSegment(sketch, "E324", {"start": v(228.49, 849.96) * mm, "end": v(230.72, 839.65) * mm});
            skLineSegment(sketch, "E325", {"start": v(225.67, 860.83) * mm, "end": v(228.49, 849.96) * mm});
            skLineSegment(sketch, "E326", {"start": v(222.29, 871.65) * mm, "end": v(225.67, 860.83) * mm});
            skLineSegment(sketch, "E327", {"start": v(218.45, 881.68) * mm, "end": v(222.29, 871.65) * mm});
            skLineSegment(sketch, "E328", {"start": v(214.41, 890.24) * mm, "end": v(218.45, 881.68) * mm});
            skLineSegment(sketch, "E329", {"start": v(210.4, 896.9) * mm, "end": v(214.41, 890.24) * mm});
            skLineSegment(sketch, "E330", {"start": v(206.6, 901.57) * mm, "end": v(210.4, 896.9) * mm});
            skLineSegment(sketch, "E331", {"start": v(202.96, 904.5) * mm, "end": v(206.6, 901.57) * mm});
            skLineSegment(sketch, "E332", {"start": v(199.38, 905.92) * mm, "end": v(202.96, 904.5) * mm});
            skLineSegment(sketch, "E333", {"start": v(195.54, 906) * mm, "end": v(199.38, 905.92) * mm});
            skLineSegment(sketch, "E334", {"start": v(191.2, 904.7) * mm, "end": v(195.54, 906) * mm});
            skLineSegment(sketch, "E335", {"start": v(186.04, 901.83) * mm, "end": v(191.2, 904.7) * mm});
            skLineSegment(sketch, "E336", {"start": v(180.02, 897.2) * mm, "end": v(186.04, 901.83) * mm});
            skLineSegment(sketch, "E337", {"start": v(173.24, 890.8) * mm, "end": v(180.02, 897.2) * mm});
            skLineSegment(sketch, "E338", {"start": v(166.1, 882.9) * mm, "end": v(173.24, 890.8) * mm});
            skLineSegment(sketch, "E339", {"start": v(159.04, 874.04) * mm, "end": v(166.1, 882.9) * mm});
            skLineSegment(sketch, "E340", {"start": v(152.49, 864.87) * mm, "end": v(159.04, 874.04) * mm});
            skLineSegment(sketch, "E341", {"start": v(146.67, 855.98) * mm, "end": v(152.49, 864.87) * mm});
            skLineSegment(sketch, "E342", {"start": v(141.5, 847.7) * mm, "end": v(146.67, 855.98) * mm});
            skLineSegment(sketch, "E343", {"start": v(136.8, 840.05) * mm, "end": v(141.5, 847.7) * mm});
            skLineSegment(sketch, "E344", {"start": v(132.22, 833.07) * mm, "end": v(136.8, 840.05) * mm});
            skLineSegment(sketch, "E345", {"start": v(127.5, 826.74) * mm, "end": v(132.22, 833.07) * mm});
            skLineSegment(sketch, "E346", {"start": v(122.42, 821.33) * mm, "end": v(127.5, 826.74) * mm});
            skLineSegment(sketch, "E347", {"start": v(116.88, 817.32) * mm, "end": v(122.42, 821.33) * mm});
            skLineSegment(sketch, "E348", {"start": v(111.06, 815.24) * mm, "end": v(116.88, 817.32) * mm});
            skLineSegment(sketch, "E349", {"start": v(105.17, 815.42) * mm, "end": v(111.06, 815.24) * mm});
            skLineSegment(sketch, "E350", {"start": v(99.56, 817.88) * mm, "end": v(105.17, 815.42) * mm});
            skLineSegment(sketch, "E351", {"start": v(94.5, 822.33) * mm, "end": v(99.56, 817.88) * mm});
            skLineSegment(sketch, "E352", {"start": v(90.03, 828.14) * mm, "end": v(94.5, 822.33) * mm});
            skLineSegment(sketch, "E353", {"start": v(86.1, 834.92) * mm, "end": v(90.03, 828.14) * mm});
            skLineSegment(sketch, "E354", {"start": v(82.46, 842.34) * mm, "end": v(86.1, 834.92) * mm});
            skLineSegment(sketch, "E355", {"start": v(74.82, 859.15) * mm, "end": v(82.46, 842.34) * mm});
            skLineSegment(sketch, "E356", {"start": v(70.27, 868.63) * mm, "end": v(74.82, 859.15) * mm});
            skLineSegment(sketch, "E357", {"start": v(65.06, 878.5) * mm, "end": v(70.27, 868.63) * mm});
            skLineSegment(sketch, "E358", {"start": v(59.32, 888.26) * mm, "end": v(65.06, 878.5) * mm});
            skLineSegment(sketch, "E359", {"start": v(53.3, 897.2) * mm, "end": v(59.32, 888.26) * mm});
            skLineSegment(sketch, "E360", {"start": v(47.4, 904.7) * mm, "end": v(53.3, 897.2) * mm});
            skLineSegment(sketch, "E361", {"start": v(41.95, 910.39) * mm, "end": v(47.4, 904.7) * mm});
            skLineSegment(sketch, "E362", {"start": v(37.1, 914.2) * mm, "end": v(41.95, 910.39) * mm});
            skLineSegment(sketch, "E363", {"start": v(32.83, 916.33) * mm, "end": v(37.1, 914.2) * mm});
            skLineSegment(sketch, "E364", {"start": v(28.94, 917) * mm, "end": v(32.83, 916.33) * mm});
            skLineSegment(sketch, "E365", {"start": v(25.18, 916.28) * mm, "end": v(28.94, 917) * mm});
            skLineSegment(sketch, "E366", {"start": v(21.22, 914.1) * mm, "end": v(25.18, 916.28) * mm});
            skLineSegment(sketch, "E367", {"start": v(16.9, 910.2) * mm, "end": v(21.22, 914.1) * mm});
            skLineSegment(sketch, "E368", {"start": v(12.15, 904.44) * mm, "end": v(16.9, 910.2) * mm});
            skLineSegment(sketch, "E369", {"start": v(7.07, 896.8) * mm, "end": v(12.15, 904.44) * mm});
            skLineSegment(sketch, "E370", {"start": v(1.97, 887.58) * mm, "end": v(7.07, 896.8) * mm});
            skLineSegment(sketch, "E371", {"start": v(-2.86, 877.4) * mm, "end": v(1.97, 887.58) * mm});
            skLineSegment(sketch, "E372", {"start": v(-7.18, 866.98) * mm, "end": v(-2.86, 877.4) * mm});
            skLineSegment(sketch, "E373", {"start": v(-10.86, 856.95) * mm, "end": v(-7.18, 866.98) * mm});
            skLineSegment(sketch, "E374", {"start": v(-14.03, 847.62) * mm, "end": v(-10.86, 856.95) * mm});
            skLineSegment(sketch, "E375", {"start": v(-16.93, 839.04) * mm, "end": v(-14.03, 847.62) * mm});
            skLineSegment(sketch, "E376", {"start": v(-19.8, 831.11) * mm, "end": v(-16.93, 839.04) * mm});
            skLineSegment(sketch, "E377", {"start": v(-22.95, 823.82) * mm, "end": v(-19.8, 831.11) * mm});
            skLineSegment(sketch, "E378", {"start": v(-26.66, 817.35) * mm, "end": v(-22.95, 823.82) * mm});
            skLineSegment(sketch, "E379", {"start": v(-31.05, 812.11) * mm, "end": v(-26.66, 817.35) * mm});
            skLineSegment(sketch, "E380", {"start": v(-36.18, 808.63) * mm, "end": v(-31.05, 812.11) * mm});
            skLineSegment(sketch, "E381", {"start": v(-41.9, 807.34) * mm, "end": v(-36.18, 808.63) * mm});
            skLineSegment(sketch, "E382", {"start": v(-47.87, 808.3) * mm, "end": v(-41.9, 807.34) * mm});
            skLineSegment(sketch, "E383", {"start": v(-53.8, 811.33) * mm, "end": v(-47.87, 808.3) * mm});
            skLineSegment(sketch, "E384", {"start": v(-59.47, 815.9) * mm, "end": v(-53.8, 811.33) * mm});
            skLineSegment(sketch, "E385", {"start": v(-64.88, 821.54) * mm, "end": v(-59.47, 815.9) * mm});
            skLineSegment(sketch, "E386", {"start": v(-70.14, 827.91) * mm, "end": v(-64.88, 821.54) * mm});
            skLineSegment(sketch, "E387", {"start": v(-75.55, 834.9) * mm, "end": v(-70.14, 827.91) * mm});
            skLineSegment(sketch, "E388", {"start": v(-81.4, 842.52) * mm, "end": v(-75.55, 834.9) * mm});
            skLineSegment(sketch, "E389", {"start": v(-87.9, 850.7) * mm, "end": v(-81.4, 842.52) * mm});
            skLineSegment(sketch, "E390", {"start": v(-95.11, 859.18) * mm, "end": v(-87.9, 850.7) * mm});
            skLineSegment(sketch, "E391", {"start": v(-102.83, 867.4) * mm, "end": v(-95.11, 859.18) * mm});
            skLineSegment(sketch, "E392", {"start": v(-110.68, 874.85) * mm, "end": v(-102.83, 867.4) * mm});
            skLineSegment(sketch, "E393", {"start": v(-118.1, 880.95) * mm, "end": v(-110.68, 874.85) * mm});
            skLineSegment(sketch, "E394", {"start": v(-124.75, 885.4) * mm, "end": v(-118.1, 880.95) * mm});
            skLineSegment(sketch, "E395", {"start": v(-130.4, 888.19) * mm, "end": v(-124.75, 885.4) * mm});
            skLineSegment(sketch, "E396", {"start": v(-135.12, 889.43) * mm, "end": v(-130.4, 888.19) * mm});
            skLineSegment(sketch, "E397", {"start": v(-139.13, 889.28) * mm, "end": v(-135.12, 889.43) * mm});
            skLineSegment(sketch, "E398", {"start": v(-142.7, 887.83) * mm, "end": v(-139.13, 889.28) * mm});
            skLineSegment(sketch, "E399", {"start": v(-146.09, 884.91) * mm, "end": v(-142.7, 887.83) * mm});
            skLineSegment(sketch, "E400", {"start": v(-149.47, 880.29) * mm, "end": v(-146.09, 884.91) * mm});
            skLineSegment(sketch, "E401", {"start": v(-152.82, 873.73) * mm, "end": v(-149.47, 880.29) * mm});
            skLineSegment(sketch, "E402", {"start": v(-156.04, 865.28) * mm, "end": v(-152.82, 873.73) * mm});
            skLineSegment(sketch, "E403", {"start": v(-159, 855.27) * mm, "end": v(-156.04, 865.28) * mm});
            skLineSegment(sketch, "E404", {"start": v(-161.46, 844.35) * mm, "end": v(-159, 855.27) * mm});
            skLineSegment(sketch, "E405", {"start": v(-163.39, 833.25) * mm, "end": v(-161.46, 844.35) * mm});
            skLineSegment(sketch, "E406", {"start": v(-164.8, 822.6) * mm, "end": v(-163.39, 833.25) * mm});
            skLineSegment(sketch, "E407", {"start": v(-166.84, 803.6) * mm, "end": v(-164.8, 822.6) * mm});
            skLineSegment(sketch, "E408", {"start": v(-167.9, 795.17) * mm, "end": v(-166.84, 803.6) * mm});
            skLineSegment(sketch, "E409", {"start": v(-169.38, 787.32) * mm, "end": v(-167.9, 795.17) * mm});
            skLineSegment(sketch, "E410", {"start": v(-171.51, 780.16) * mm, "end": v(-169.38, 787.32) * mm});
            skLineSegment(sketch, "E411", {"start": v(-174.61, 774.01) * mm, "end": v(-171.51, 780.16) * mm});
            skLineSegment(sketch, "E412", {"start": v(-178.78, 769.42) * mm, "end": v(-174.61, 774.01) * mm});
            skLineSegment(sketch, "E413", {"start": v(-183.96, 766.78) * mm, "end": v(-178.78, 769.42) * mm});
            skLineSegment(sketch, "E414", {"start": v(-189.93, 766.27) * mm, "end": v(-183.96, 766.78) * mm});
            skLineSegment(sketch, "E415", {"start": v(-196.33, 767.77) * mm, "end": v(-189.93, 766.27) * mm});
            skLineSegment(sketch, "E416", {"start": v(-202.86, 770.9) * mm, "end": v(-196.33, 767.77) * mm});
            skLineSegment(sketch, "E417", {"start": v(-209.36, 775.13) * mm, "end": v(-202.86, 770.9) * mm});
            skLineSegment(sketch, "E418", {"start": v(-215.91, 780.16) * mm, "end": v(-209.36, 775.13) * mm});
            skLineSegment(sketch, "E419", {"start": v(-222.72, 785.8) * mm, "end": v(-215.91, 780.16) * mm});
            skLineSegment(sketch, "E420", {"start": v(-230.06, 791.97) * mm, "end": v(-222.72, 785.8) * mm});
            skLineSegment(sketch, "E421", {"start": v(-238.14, 798.53) * mm, "end": v(-230.06, 791.97) * mm});
            skLineSegment(sketch, "E422", {"start": v(-246.95, 805.23) * mm, "end": v(-238.14, 798.53) * mm});
            skLineSegment(sketch, "E423", {"start": v(-256.22, 811.66) * mm, "end": v(-246.95, 805.23) * mm});
            skLineSegment(sketch, "E424", {"start": v(-265.47, 817.3) * mm, "end": v(-256.22, 811.66) * mm});
            skLineSegment(sketch, "E425", {"start": v(-274.05, 821.74) * mm, "end": v(-265.47, 817.3) * mm});
            skLineSegment(sketch, "E426", {"start": v(-281.57, 824.79) * mm, "end": v(-274.05, 821.74) * mm});
            skLineSegment(sketch, "E427", {"start": v(-287.8, 826.41) * mm, "end": v(-281.57, 824.79) * mm});
            skLineSegment(sketch, "E428", {"start": v(-292.8, 826.7) * mm, "end": v(-287.8, 826.41) * mm});
            skLineSegment(sketch, "E429", {"start": v(-296.76, 825.78) * mm, "end": v(-292.8, 826.7) * mm});
            skLineSegment(sketch, "E430", {"start": v(-300.01, 823.65) * mm, "end": v(-296.76, 825.78) * mm});
            skLineSegment(sketch, "E431", {"start": v(-302.76, 820.14) * mm, "end": v(-300.01, 823.65) * mm});
            skLineSegment(sketch, "E432", {"start": v(-305.07, 815) * mm, "end": v(-302.76, 820.14) * mm});
            skLineSegment(sketch, "E433", {"start": v(-306.97, 808.02) * mm, "end": v(-305.07, 815) * mm});
            skLineSegment(sketch, "E434", {"start": v(-308.34, 799.19) * mm, "end": v(-306.97, 808.02) * mm});
            skLineSegment(sketch, "E435", {"start": v(-309.1, 788.9) * mm, "end": v(-308.34, 799.19) * mm});
            skLineSegment(sketch, "E436", {"start": v(-309.2, 777.77) * mm, "end": v(-309.1, 788.9) * mm});
            skLineSegment(sketch, "E437", {"start": v(-308.75, 766.52) * mm, "end": v(-309.2, 777.77) * mm});
            skLineSegment(sketch, "E438", {"start": v(-307.91, 755.78) * mm, "end": v(-308.75, 766.52) * mm});
            skLineSegment(sketch, "E439", {"start": v(-306.87, 745.8) * mm, "end": v(-307.91, 755.78) * mm});
            skLineSegment(sketch, "E440", {"start": v(-305.88, 736.63) * mm, "end": v(-306.87, 745.8) * mm});
            skLineSegment(sketch, "E441", {"start": v(-305.14, 728.1) * mm, "end": v(-305.88, 736.63) * mm});
            skLineSegment(sketch, "E442", {"start": v(-304.89, 720.04) * mm, "end": v(-305.14, 728.1) * mm});
            skLineSegment(sketch, "E443", {"start": v(-305.42, 712.55) * mm, "end": v(-304.89, 720.04) * mm});
            skLineSegment(sketch, "E444", {"start": v(-307.05, 705.84) * mm, "end": v(-305.42, 712.55) * mm});
            skLineSegment(sketch, "E445", {"start": v(-310.05, 700.4) * mm, "end": v(-307.05, 705.84) * mm});
            skLineSegment(sketch, "E446", {"start": v(-314.44, 696.62) * mm, "end": v(-310.05, 700.4) * mm});
            skLineSegment(sketch, "E447", {"start": v(-320.05, 694.74) * mm, "end": v(-314.44, 696.62) * mm});
            skLineSegment(sketch, "E448", {"start": v(-326.56, 694.74) * mm, "end": v(-320.05, 694.74) * mm});
            skLineSegment(sketch, "E449", {"start": v(-333.57, 696.3) * mm, "end": v(-326.56, 694.74) * mm});
            skLineSegment(sketch, "E450", {"start": v(-340.83, 699) * mm, "end": v(-333.57, 696.3) * mm});
            skLineSegment(sketch, "E451", {"start": v(-348.3, 702.51) * mm, "end": v(-340.83, 699) * mm});
            skLineSegment(sketch, "E452", {"start": v(-356.12, 706.58) * mm, "end": v(-348.3, 702.51) * mm});
            skLineSegment(sketch, "E453", {"start": v(-364.58, 711.05) * mm, "end": v(-356.12, 706.58) * mm});
            skLineSegment(sketch, "E454", {"start": v(-373.8, 715.77) * mm, "end": v(-364.58, 711.05) * mm});
            skLineSegment(sketch, "E455", {"start": v(-383.78, 720.5) * mm, "end": v(-373.8, 715.77) * mm});
            skLineSegment(sketch, "E456", {"start": v(-394.14, 724.87) * mm, "end": v(-383.78, 720.5) * mm});
            skLineSegment(sketch, "E457", {"start": v(-404.33, 728.55) * mm, "end": v(-394.14, 724.87) * mm});
            skLineSegment(sketch, "E458", {"start": v(-413.73, 731.22) * mm, "end": v(-404.33, 728.55) * mm});
            skLineSegment(sketch, "E459", {"start": v(-421.8, 732.71) * mm, "end": v(-413.73, 731.22) * mm});
            skLineSegment(sketch, "E460", {"start": v(-428.36, 733.1) * mm, "end": v(-421.8, 732.71) * mm});
            skLineSegment(sketch, "E461", {"start": v(-433.41, 732.43) * mm, "end": v(-428.36, 733.1) * mm});
            skLineSegment(sketch, "E462", {"start": v(-437.22, 730.76) * mm, "end": v(-433.41, 732.43) * mm});
            skLineSegment(sketch, "E463", {"start": v(-440.04, 728.07) * mm, "end": v(-437.22, 730.76) * mm});
            skLineSegment(sketch, "E464", {"start": v(-442.05, 724.13) * mm, "end": v(-440.04, 728.07) * mm});
            skLineSegment(sketch, "E465", {"start": v(-443.32, 718.72) * mm, "end": v(-442.05, 724.13) * mm});
            skLineSegment(sketch, "E466", {"start": v(-443.78, 711.6) * mm, "end": v(-443.32, 718.72) * mm});
            skLineSegment(sketch, "E467", {"start": v(-443.34, 702.82) * mm, "end": v(-443.78, 711.6) * mm});
            skLineSegment(sketch, "E468", {"start": v(-442.02, 692.68) * mm, "end": v(-443.34, 702.82) * mm});
            skLineSegment(sketch, "E469", {"start": v(-439.89, 681.84) * mm, "end": v(-442.02, 692.68) * mm});
            skLineSegment(sketch, "E470", {"start": v(-437.15, 670.92) * mm, "end": v(-439.89, 681.84) * mm});
            skLineSegment(sketch, "E471", {"start": v(-434.12, 660.53) * mm, "end": v(-437.15, 670.92) * mm});
            skLineSegment(sketch, "E472", {"start": v(-431.08, 650.9) * mm, "end": v(-434.12, 660.53) * mm});
            skLineSegment(sketch, "E473", {"start": v(-428.2, 642.04) * mm, "end": v(-431.08, 650.9) * mm});
            skLineSegment(sketch, "E474", {"start": v(-425.72, 633.76) * mm, "end": v(-428.2, 642.04) * mm});
            skLineSegment(sketch, "E475", {"start": v(-423.79, 625.88) * mm, "end": v(-425.72, 633.76) * mm});
            skLineSegment(sketch, "E476", {"start": v(-422.72, 618.41) * mm, "end": v(-423.79, 625.88) * mm});
            skLineSegment(sketch, "E477", {"start": v(-422.87, 611.48) * mm, "end": v(-422.72, 618.41) * mm});
            skLineSegment(sketch, "E478", {"start": v(-424.57, 605.49) * mm, "end": v(-422.87, 611.48) * mm});
            skLineSegment(sketch, "E479", {"start": v(-427.98, 600.81) * mm, "end": v(-424.57, 605.49) * mm});
            skLineSegment(sketch, "E480", {"start": v(-432.96, 597.74) * mm, "end": v(-427.98, 600.81) * mm});
            skLineSegment(sketch, "E481", {"start": v(-439.23, 596.32) * mm, "end": v(-432.96, 597.74) * mm});
            skLineSegment(sketch, "E482", {"start": v(-446.34, 596.32) * mm, "end": v(-439.23, 596.32) * mm});
            skLineSegment(sketch, "E483", {"start": v(-453.99, 597.43) * mm, "end": v(-446.34, 596.32) * mm});
            skLineSegment(sketch, "E484", {"start": v(-462.01, 599.29) * mm, "end": v(-453.99, 597.43) * mm});
            skLineSegment(sketch, "E485", {"start": v(-470.5, 601.65) * mm, "end": v(-462.01, 599.29) * mm});
            skLineSegment(sketch, "E486", {"start": v(-479.64, 604.3) * mm, "end": v(-470.5, 601.65) * mm});
            skLineSegment(sketch, "E487", {"start": v(-489.6, 607.06) * mm, "end": v(-479.64, 604.3) * mm});
            skLineSegment(sketch, "E488", {"start": v(-500.27, 609.73) * mm, "end": v(-489.6, 607.06) * mm});
            skLineSegment(sketch, "E489", {"start": v(-511.26, 611.96) * mm, "end": v(-500.27, 609.73) * mm});
            skLineSegment(sketch, "E490", {"start": v(-522, 613.59) * mm, "end": v(-511.26, 611.96) * mm});
            skLineSegment(sketch, "E491", {"start": v(-531.79, 614.38) * mm, "end": v(-522, 613.59) * mm});
            skLineSegment(sketch, "E492", {"start": v(-540.12, 614.32) * mm, "end": v(-531.79, 614.38) * mm});
            skLineSegment(sketch, "E493", {"start": v(-546.75, 613.44) * mm, "end": v(-540.12, 614.32) * mm});
            skLineSegment(sketch, "E494", {"start": v(-551.7, 611.8) * mm, "end": v(-546.75, 613.44) * mm});
            skLineSegment(sketch, "E495", {"start": v(-555.23, 609.47) * mm, "end": v(-551.7, 611.8) * mm});
            skLineSegment(sketch, "E496", {"start": v(-557.54, 606.3) * mm, "end": v(-555.23, 609.47) * mm});
            skLineSegment(sketch, "E497", {"start": v(-558.81, 602.1) * mm, "end": v(-557.54, 606.3) * mm});
            skLineSegment(sketch, "E498", {"start": v(-559.02, 596.62) * mm, "end": v(-558.81, 602.1) * mm});
            skLineSegment(sketch, "E499", {"start": v(-558.13, 589.64) * mm, "end": v(-559.02, 596.62) * mm});
            skLineSegment(sketch, "E500", {"start": v(-556.02, 581.23) * mm, "end": v(-558.13, 589.64) * mm});
            skLineSegment(sketch, "E501", {"start": v(-552.77, 571.68) * mm, "end": v(-556.02, 581.23) * mm});
            skLineSegment(sketch, "E502", {"start": v(-548.58, 561.5) * mm, "end": v(-552.77, 571.68) * mm});
            skLineSegment(sketch, "E503", {"start": v(-543.78, 551.36) * mm, "end": v(-548.58, 561.5) * mm});
            skLineSegment(sketch, "E504", {"start": v(-538.75, 541.7) * mm, "end": v(-543.78, 551.36) * mm});
            skLineSegment(sketch, "E505", {"start": v(-533.82, 532.82) * mm, "end": v(-538.75, 541.7) * mm});
            skLineSegment(sketch, "E506", {"start": v(-529.22, 524.61) * mm, "end": v(-533.82, 532.82) * mm});
            skLineSegment(sketch, "E507", {"start": v(-525.1, 516.94) * mm, "end": v(-529.22, 524.61) * mm});
            skLineSegment(sketch, "E508", {"start": v(-521.63, 509.57) * mm, "end": v(-525.1, 516.94) * mm});
            skLineSegment(sketch, "E509", {"start": v(-519.04, 502.41) * mm, "end": v(-521.63, 509.57) * mm});
            skLineSegment(sketch, "E510", {"start": v(-517.74, 495.6) * mm, "end": v(-519.04, 502.41) * mm});
            skLineSegment(sketch, "E511", {"start": v(-518.12, 489.36) * mm, "end": v(-517.74, 495.6) * mm});
            skLineSegment(sketch, "E512", {"start": v(-520.38, 484.05) * mm, "end": v(-518.12, 489.36) * mm});
            skLineSegment(sketch, "E513", {"start": v(-524.52, 479.98) * mm, "end": v(-520.38, 484.05) * mm});
            skLineSegment(sketch, "E514", {"start": v(-530.26, 477.27) * mm, "end": v(-524.52, 479.98) * mm});
            skLineSegment(sketch, "E515", {"start": v(-537.17, 475.8) * mm, "end": v(-530.26, 477.27) * mm});
            skLineSegment(sketch, "E516", {"start": v(-544.82, 475.31) * mm, "end": v(-537.17, 475.8) * mm});
            skLineSegment(sketch, "E517", {"start": v(-553.05, 475.51) * mm, "end": v(-544.82, 475.31) * mm});
            skLineSegment(sketch, "E518", {"start": v(-561.8, 476.12) * mm, "end": v(-553.05, 475.51) * mm});
            skLineSegment(sketch, "E519", {"start": v(-571.28, 476.94) * mm, "end": v(-561.8, 476.12) * mm});
            skLineSegment(sketch, "E520", {"start": v(-581.55, 477.72) * mm, "end": v(-571.28, 476.94) * mm});
            skLineSegment(sketch, "E521", {"start": v(-592.5, 478.26) * mm, "end": v(-581.55, 477.72) * mm});
            skLineSegment(sketch, "E522", {"start": v(-603.7, 478.38) * mm, "end": v(-592.5, 478.26) * mm});
            skLineSegment(sketch, "E523", {"start": v(-614.57, 477.93) * mm, "end": v(-603.7, 478.38) * mm});
            skLineSegment(sketch, "E524", {"start": v(-624.4, 476.86) * mm, "end": v(-614.57, 477.93) * mm});
            skLineSegment(sketch, "E525", {"start": v(-632.68, 475.26) * mm, "end": v(-624.4, 476.86) * mm});
            skLineSegment(sketch, "E526", {"start": v(-639.13, 473.15) * mm, "end": v(-632.68, 475.26) * mm});
            skLineSegment(sketch, "E527", {"start": v(-643.83, 470.61) * mm, "end": v(-639.13, 473.15) * mm});
            skLineSegment(sketch, "E528", {"start": v(-646.95, 467.64) * mm, "end": v(-643.83, 470.61) * mm});
            skLineSegment(sketch, "E529", {"start": v(-648.7, 464.1) * mm, "end": v(-646.95, 467.64) * mm});
            skLineSegment(sketch, "E530", {"start": v(-649.21, 459.8) * mm, "end": v(-648.7, 464.1) * mm});
            skLineSegment(sketch, "E531", {"start": v(-648.47, 454.4) * mm, "end": v(-649.21, 459.8) * mm});
            skLineSegment(sketch, "E532", {"start": v(-646.32, 447.85) * mm, "end": v(-648.47, 454.4) * mm});
            skLineSegment(sketch, "E533", {"start": v(-642.73, 440.08) * mm, "end": v(-646.32, 447.85) * mm});
            skLineSegment(sketch, "E534", {"start": v(-637.78, 431.4) * mm, "end": v(-642.73, 440.08) * mm});
            skLineSegment(sketch, "E535", {"start": v(-631.76, 422.28) * mm, "end": v(-637.78, 431.4) * mm});
            skLineSegment(sketch, "E536", {"start": v(-625.13, 413.23) * mm, "end": v(-631.76, 422.28) * mm});
            skLineSegment(sketch, "E537", {"start": v(-618.35, 404.7) * mm, "end": v(-625.13, 413.23) * mm});
            skLineSegment(sketch, "E538", {"start": v(-611.8, 396.82) * mm, "end": v(-618.35, 404.7) * mm});
            skLineSegment(sketch, "E539", {"start": v(-605.68, 389.61) * mm, "end": v(-611.8, 396.82) * mm});
            skLineSegment(sketch, "E540", {"start": v(-600.11, 382.8) * mm, "end": v(-605.68, 389.61) * mm});
            skLineSegment(sketch, "E541", {"start": v(-595.24, 376.2) * mm, "end": v(-600.11, 382.8) * mm});
            skLineSegment(sketch, "E542", {"start": v(-591.27, 369.67) * mm, "end": v(-595.24, 376.2) * mm});
            skLineSegment(sketch, "E543", {"start": v(-588.6, 363.22) * mm, "end": v(-591.27, 369.67) * mm});
            skLineSegment(sketch, "E544", {"start": v(-587.64, 357.02) * mm, "end": v(-588.6, 363.22) * mm});
            skLineSegment(sketch, "E545", {"start": v(-588.7, 351.36) * mm, "end": v(-587.64, 357.02) * mm});
            skLineSegment(sketch, "E546", {"start": v(-591.86, 346.53) * mm, "end": v(-588.7, 351.36) * mm});
            skLineSegment(sketch, "E547", {"start": v(-596.84, 342.72) * mm, "end": v(-591.86, 346.53) * mm});
            skLineSegment(sketch, "E548", {"start": v(-603.24, 339.88) * mm, "end": v(-596.84, 342.72) * mm});
            skLineSegment(sketch, "E549", {"start": v(-610.6, 337.9) * mm, "end": v(-603.24, 339.88) * mm});
            skLineSegment(sketch, "E550", {"start": v(-618.68, 336.5) * mm, "end": v(-610.6, 337.9) * mm});
            skLineSegment(sketch, "E551", {"start": v(-627.4, 335.4) * mm, "end": v(-618.68, 336.5) * mm});
            skLineSegment(sketch, "E552", {"start": v(-636.82, 334.4) * mm, "end": v(-627.4, 335.4) * mm});
            skLineSegment(sketch, "E553", {"start": v(-647, 333.25) * mm, "end": v(-636.82, 334.4) * mm});
            skLineSegment(sketch, "E554", {"start": v(-657.82, 331.75) * mm, "end": v(-647, 333.25) * mm});
            skLineSegment(sketch, "E555", {"start": v(-668.85, 329.8) * mm, "end": v(-657.82, 331.75) * mm});
            skLineSegment(sketch, "E556", {"start": v(-679.46, 327.36) * mm, "end": v(-668.85, 329.8) * mm});
            skLineSegment(sketch, "E557", {"start": v(-688.99, 324.54) * mm, "end": v(-679.46, 327.36) * mm});
            skLineSegment(sketch, "E558", {"start": v(-696.94, 321.41) * mm, "end": v(-688.99, 324.54) * mm});
            skLineSegment(sketch, "E559", {"start": v(-703.03, 318.16) * mm, "end": v(-696.94, 321.41) * mm});
            skLineSegment(sketch, "E560", {"start": v(-707.3, 314.78) * mm, "end": v(-703.03, 318.16) * mm});
            skLineSegment(sketch, "E561", {"start": v(-709.94, 311.28) * mm, "end": v(-707.3, 314.78) * mm});
            skLineSegment(sketch, "E562", {"start": v(-711.11, 307.47) * mm, "end": v(-709.94, 311.28) * mm});
            skLineSegment(sketch, "E563", {"start": v(-710.9, 303.15) * mm, "end": v(-711.11, 307.47) * mm});
            skLineSegment(sketch, "E564", {"start": v(-709.26, 298.07) * mm, "end": v(-710.9, 303.15) * mm});
            skLineSegment(sketch, "E565", {"start": v(-706, 292.07) * mm, "end": v(-709.26, 298.07) * mm});
            skLineSegment(sketch, "E566", {"start": v(-701.13, 285.2) * mm, "end": v(-706, 292.07) * mm});
            skLineSegment(sketch, "E567", {"start": v(-694.75, 277.62) * mm, "end": v(-701.13, 285.2) * mm});
            skLineSegment(sketch, "E568", {"start": v(-687.24, 269.82) * mm, "end": v(-694.75, 277.62) * mm});
            skLineSegment(sketch, "E569", {"start": v(-679.06, 262.18) * mm, "end": v(-687.24, 269.82) * mm});
            skLineSegment(sketch, "E570", {"start": v(-670.8, 255) * mm, "end": v(-679.06, 262.18) * mm});
            skLineSegment(sketch, "E571", {"start": v(-662.85, 248.44) * mm, "end": v(-670.8, 255) * mm});
            skLineSegment(sketch, "E572", {"start": v(-655.43, 242.42) * mm, "end": v(-662.85, 248.44) * mm});
            skLineSegment(sketch, "E573", {"start": v(-648.65, 236.73) * mm, "end": v(-655.43, 242.42) * mm});
            skLineSegment(sketch, "E574", {"start": v(-642.58, 231.11) * mm, "end": v(-648.65, 236.73) * mm});
            skLineSegment(sketch, "E575", {"start": v(-637.43, 225.43) * mm, "end": v(-642.58, 231.11) * mm});
            skLineSegment(sketch, "E576", {"start": v(-633.51, 219.6) * mm, "end": v(-637.43, 225.43) * mm});
            skLineSegment(sketch, "E577", {"start": v(-631.33, 213.7) * mm, "end": v(-633.51, 219.6) * mm});
            skLineSegment(sketch, "E578", {"start": v(-631.18, 207.95) * mm, "end": v(-631.33, 213.7) * mm});
            skLineSegment(sketch, "E579", {"start": v(-633.23, 202.62) * mm, "end": v(-631.18, 207.95) * mm});
            skLineSegment(sketch, "E580", {"start": v(-637.27, 197.9) * mm, "end": v(-633.23, 202.62) * mm});
            skLineSegment(sketch, "E581", {"start": v(-642.91, 193.9) * mm, "end": v(-637.27, 197.9) * mm});
            skLineSegment(sketch, "E582", {"start": v(-649.74, 190.53) * mm, "end": v(-642.91, 193.9) * mm});
            skLineSegment(sketch, "E583", {"start": v(-657.4, 187.63) * mm, "end": v(-649.74, 190.53) * mm});
            skLineSegment(sketch, "E584", {"start": v(-665.72, 184.94) * mm, "end": v(-657.4, 187.63) * mm});
            skLineSegment(sketch, "E585", {"start": v(-674.76, 182.22) * mm, "end": v(-665.72, 184.94) * mm});
            skLineSegment(sketch, "E586", {"start": v(-684.54, 179.22) * mm, "end": v(-674.76, 182.22) * mm});
            skLineSegment(sketch, "E587", {"start": v(-694.86, 175.82) * mm, "end": v(-684.54, 179.22) * mm});
            skLineSegment(sketch, "E588", {"start": v(-705.35, 171.93) * mm, "end": v(-694.86, 175.82) * mm});
            skLineSegment(sketch, "E589", {"start": v(-715.35, 167.67) * mm, "end": v(-705.35, 171.93) * mm});
            skLineSegment(sketch, "E590", {"start": v(-724.32, 163.17) * mm, "end": v(-715.35, 167.67) * mm});
            skLineSegment(sketch, "E591", {"start": v(-731.69, 158.67) * mm, "end": v(-724.32, 163.17) * mm});
            skLineSegment(sketch, "E592", {"start": v(-737.22, 154.33) * mm, "end": v(-731.69, 158.67) * mm});
            skLineSegment(sketch, "E593", {"start": v(-740.96, 150.22) * mm, "end": v(-737.22, 154.33) * mm});
            skLineSegment(sketch, "E594", {"start": v(-743.01, 146.28) * mm, "end": v(-740.96, 150.22) * mm});
            skLineSegment(sketch, "E595", {"start": v(-743.6, 142.3) * mm, "end": v(-743.01, 146.28) * mm});
            skLineSegment(sketch, "E596", {"start": v(-742.68, 138.07) * mm, "end": v(-743.6, 142.3) * mm});
            skLineSegment(sketch, "E597", {"start": v(-740.24, 133.4) * mm, "end": v(-742.68, 138.07) * mm});
            skLineSegment(sketch, "E598", {"start": v(-736.08, 128.14) * mm, "end": v(-740.24, 133.4) * mm});
            skLineSegment(sketch, "E599", {"start": v(-730.16, 122.3) * mm, "end": v(-736.08, 128.14) * mm});
            skLineSegment(sketch, "E600", {"start": v(-722.64, 116.08) * mm, "end": v(-730.16, 122.3) * mm});
            skLineSegment(sketch, "E601", {"start": v(-713.9, 109.78) * mm, "end": v(-722.64, 116.08) * mm});
            skLineSegment(sketch, "E602", {"start": v(-704.5, 103.7) * mm, "end": v(-713.9, 109.78) * mm});
            skLineSegment(sketch, "E603", {"start": v(-695.08, 98.12) * mm, "end": v(-704.5, 103.7) * mm});
            skLineSegment(sketch, "E604", {"start": v(-686.04, 93.04) * mm, "end": v(-695.08, 98.12) * mm});
            skLineSegment(sketch, "E605", {"start": v(-677.6, 88.4) * mm, "end": v(-686.04, 93.04) * mm});
            skLineSegment(sketch, "E606", {"start": v(-669.86, 84) * mm, "end": v(-677.6, 88.4) * mm});
            skLineSegment(sketch, "E607", {"start": v(-662.83, 79.55) * mm, "end": v(-669.86, 84) * mm});
            skLineSegment(sketch, "E608", {"start": v(-656.65, 74.9) * mm, "end": v(-662.83, 79.55) * mm});
            skLineSegment(sketch, "E609", {"start": v(-651.68, 69.88) * mm, "end": v(-656.65, 74.9) * mm});
            skLineSegment(sketch, "E610", {"start": v(-648.35, 64.52) * mm, "end": v(-651.68, 69.88) * mm});
            skLineSegment(sketch, "E611", {"start": v(-647.05, 58.9) * mm, "end": v(-648.35, 64.52) * mm});
            skLineSegment(sketch, "E612", {"start": v(-647.94, 53.31) * mm, "end": v(-647.05, 58.9) * mm});
            skLineSegment(sketch, "E613", {"start": v(-650.91, 47.96) * mm, "end": v(-647.94, 53.31) * mm});
            skLineSegment(sketch, "E614", {"start": v(-655.66, 42.98) * mm, "end": v(-650.91, 47.96) * mm});
            skLineSegment(sketch, "E615", {"start": v(-661.68, 38.4) * mm, "end": v(-655.66, 42.98) * mm});
            skLineSegment(sketch, "E616", {"start": v(-668.64, 34.16) * mm, "end": v(-661.68, 38.4) * mm});
            skLineSegment(sketch, "E617", {"start": v(-676.34, 30.02) * mm, "end": v(-668.64, 34.16) * mm});
            skLineSegment(sketch, "E618", {"start": v(-684.72, 25.73) * mm, "end": v(-676.34, 30.02) * mm});
            skLineSegment(sketch, "E619", {"start": v(-693.76, 21.06) * mm, "end": v(-684.72, 25.73) * mm});
            skLineSegment(sketch, "E620", {"start": v(-703.31, 15.93) * mm, "end": v(-693.76, 21.06) * mm});
            skLineSegment(sketch, "E621", {"start": v(-712.91, 10.29) * mm, "end": v(-703.31, 15.93) * mm});
            skLineSegment(sketch, "E622", {"start": v(-722.08, 4.34) * mm, "end": v(-712.91, 10.29) * mm});
            skLineSegment(sketch, "E623", {"start": v(-730.19, -1.65) * mm, "end": v(-722.08, 4.34) * mm});
            skLineSegment(sketch, "E624", {"start": v(-736.77, -7.4) * mm, "end": v(-730.19, -1.65) * mm});
            skLineSegment(sketch, "E625", {"start": v(-741.6, -12.67) * mm, "end": v(-736.77, -7.4) * mm});
            skLineSegment(sketch, "E626", {"start": v(-744.66, -17.42) * mm, "end": v(-741.6, -12.67) * mm});
            skLineSegment(sketch, "E627", {"start": v(-746.11, -21.72) * mm, "end": v(-744.66, -17.42) * mm});
            skLineSegment(sketch, "E628", {"start": v(-746.09, -25.76) * mm, "end": v(-746.11, -21.72) * mm});
            skLineSegment(sketch, "E629", {"start": v(-744.56, -29.77) * mm, "end": v(-746.09, -25.76) * mm});
            skLineSegment(sketch, "E630", {"start": v(-741.41, -33.93) * mm, "end": v(-744.56, -29.77) * mm});
            skLineSegment(sketch, "E631", {"start": v(-736.51, -38.38) * mm, "end": v(-741.41, -33.93) * mm});
            skLineSegment(sketch, "E632", {"start": v(-729.78, -43.05) * mm, "end": v(-736.51, -38.38) * mm});
            skLineSegment(sketch, "E633", {"start": v(-721.4, -47.83) * mm, "end": v(-729.78, -43.05) * mm});
            skLineSegment(sketch, "E634", {"start": v(-711.77, -52.5) * mm, "end": v(-721.4, -47.83) * mm});
            skLineSegment(sketch, "E635", {"start": v(-701.5, -56.85) * mm, "end": v(-711.77, -52.5) * mm});
            skLineSegment(sketch, "E636", {"start": v(-691.22, -60.73) * mm, "end": v(-701.5, -56.85) * mm});
            skLineSegment(sketch, "E637", {"start": v(-681.4, -64.19) * mm, "end": v(-691.22, -60.73) * mm});
            skLineSegment(sketch, "E638", {"start": v(-672.2, -67.3) * mm, "end": v(-681.4, -64.19) * mm});
            skLineSegment(sketch, "E639", {"start": v(-663.74, -70.33) * mm, "end": v(-672.2, -67.3) * mm});
            skLineSegment(sketch, "E640", {"start": v(-655.97, -73.46) * mm, "end": v(-663.74, -70.33) * mm});
            skLineSegment(sketch, "E641", {"start": v(-649.03, -76.96) * mm, "end": v(-655.97, -73.46) * mm});
            skLineSegment(sketch, "E642", {"start": v(-643.2, -81) * mm, "end": v(-649.03, -76.96) * mm});
            skLineSegment(sketch, "E643", {"start": v(-638.87, -85.65) * mm, "end": v(-643.2, -81) * mm});
            skLineSegment(sketch, "E644", {"start": v(-636.46, -90.88) * mm, "end": v(-638.87, -85.65) * mm});
            skLineSegment(sketch, "E645", {"start": v(-636.23, -96.52) * mm, "end": v(-636.46, -90.88) * mm});
            skLineSegment(sketch, "E646", {"start": v(-638.09, -102.29) * mm, "end": v(-636.23, -96.52) * mm});
            skLineSegment(sketch, "E647", {"start": v(-641.77, -108.03) * mm, "end": v(-638.09, -102.29) * mm});
            skLineSegment(sketch, "E648", {"start": v(-646.82, -113.56) * mm, "end": v(-641.77, -108.03) * mm});
            skLineSegment(sketch, "E649", {"start": v(-652.9, -118.97) * mm, "end": v(-646.82, -113.56) * mm});
            skLineSegment(sketch, "E650", {"start": v(-659.7, -124.4) * mm, "end": v(-652.9, -118.97) * mm});
            skLineSegment(sketch, "E651", {"start": v(-675.3, -136.2) * mm, "end": v(-659.7, -124.4) * mm});
            skLineSegment(sketch, "E652", {"start": v(-683.78, -142.88) * mm, "end": v(-675.3, -136.2) * mm});
            skLineSegment(sketch, "E653", {"start": v(-692.29, -150.04) * mm, "end": v(-683.78, -142.88) * mm});
            skLineSegment(sketch, "E654", {"start": v(-700.34, -157.43) * mm, "end": v(-692.29, -150.04) * mm});
            skLineSegment(sketch, "E655", {"start": v(-707.35, -164.72) * mm, "end": v(-700.34, -157.43) * mm});
            skLineSegment(sketch, "E656", {"start": v(-712.97, -171.53) * mm, "end": v(-707.35, -164.72) * mm});
            skLineSegment(sketch, "E657", {"start": v(-716.95, -177.62) * mm, "end": v(-712.97, -171.53) * mm});
            skLineSegment(sketch, "E658", {"start": v(-719.29, -182.88) * mm, "end": v(-716.95, -177.62) * mm});
            skLineSegment(sketch, "E659", {"start": v(-720.1, -187.43) * mm, "end": v(-719.29, -182.88) * mm});
            skLineSegment(sketch, "E660", {"start": v(-719.47, -191.47) * mm, "end": v(-720.1, -187.43) * mm});
            skLineSegment(sketch, "E661", {"start": v(-717.36, -195.17) * mm, "end": v(-719.47, -191.47) * mm});
            skLineSegment(sketch, "E662", {"start": v(-713.68, -198.78) * mm, "end": v(-717.36, -195.17) * mm});
            skLineSegment(sketch, "E663", {"start": v(-708.22, -202.31) * mm, "end": v(-713.68, -198.78) * mm});
            skLineSegment(sketch, "E664", {"start": v(-700.9, -205.77) * mm, "end": v(-708.22, -202.31) * mm});
            skLineSegment(sketch, "E665", {"start": v(-691.9, -209.04) * mm, "end": v(-700.9, -205.77) * mm});
            skLineSegment(sketch, "E666", {"start": v(-681.72, -212.01) * mm, "end": v(-691.9, -209.04) * mm});
            skLineSegment(sketch, "E667", {"start": v(-670.9, -214.58) * mm, "end": v(-681.72, -212.01) * mm});
            skLineSegment(sketch, "E668", {"start": v(-660.1, -216.69) * mm, "end": v(-670.9, -214.58) * mm});
            skLineSegment(sketch, "E669", {"start": v(-649.77, -218.44) * mm, "end": v(-660.1, -216.69) * mm});
            skLineSegment(sketch, "E670", {"start": v(-640.12, -219.99) * mm, "end": v(-649.77, -218.44) * mm});
            skLineSegment(sketch, "E671", {"start": v(-631.2, -221.54) * mm, "end": v(-640.12, -219.99) * mm});
            skLineSegment(sketch, "E672", {"start": v(-622.95, -223.3) * mm, "end": v(-631.2, -221.54) * mm});
            skLineSegment(sketch, "E673", {"start": v(-615.45, -225.55) * mm, "end": v(-622.95, -223.3) * mm});
            skLineSegment(sketch, "E674", {"start": v(-608.95, -228.47) * mm, "end": v(-615.45, -225.55) * mm});
            skLineSegment(sketch, "E675", {"start": v(-603.82, -232.28) * mm, "end": v(-608.95, -228.47) * mm});
            skLineSegment(sketch, "E676", {"start": v(-600.47, -236.96) * mm, "end": v(-603.82, -232.28) * mm});
            skLineSegment(sketch, "E677", {"start": v(-599.12, -242.4) * mm, "end": v(-600.47, -236.96) * mm});
            skLineSegment(sketch, "E678", {"start": v(-599.86, -248.36) * mm, "end": v(-599.12, -242.4) * mm});
            skLineSegment(sketch, "E679", {"start": v(-602.37, -254.6) * mm, "end": v(-599.86, -248.36) * mm});
            skLineSegment(sketch, "E680", {"start": v(-606.34, -260.9) * mm, "end": v(-602.37, -254.6) * mm});
            skLineSegment(sketch, "E681", {"start": v(-611.34, -267.28) * mm, "end": v(-606.34, -260.9) * mm});
            skLineSegment(sketch, "E682", {"start": v(-617.13, -273.79) * mm, "end": v(-611.34, -267.28) * mm});
            skLineSegment(sketch, "E683", {"start": v(-630.44, -287.99) * mm, "end": v(-617.13, -273.79) * mm});
            skLineSegment(sketch, "E684", {"start": v(-637.68, -295.94) * mm, "end": v(-630.44, -287.99) * mm});
            skLineSegment(sketch, "E685", {"start": v(-644.9, -304.4) * mm, "end": v(-637.68, -295.94) * mm});
            skLineSegment(sketch, "E686", {"start": v(-651.65, -313) * mm, "end": v(-644.9, -304.4) * mm});
            skLineSegment(sketch, "E687", {"start": v(-657.44, -321.39) * mm, "end": v(-651.65, -313) * mm});
            skLineSegment(sketch, "E688", {"start": v(-661.94, -329.08) * mm, "end": v(-657.44, -321.39) * mm});
            skLineSegment(sketch, "E689", {"start": v(-664.96, -335.81) * mm, "end": v(-661.94, -329.08) * mm});
            skLineSegment(sketch, "E690", {"start": v(-666.5, -341.48) * mm, "end": v(-664.96, -335.81) * mm});
            skLineSegment(sketch, "E691", {"start": v(-666.64, -346.18) * mm, "end": v(-666.5, -341.48) * mm});
            skLineSegment(sketch, "E692", {"start": v(-665.44, -350.11) * mm, "end": v(-666.64, -346.18) * mm});
            skLineSegment(sketch, "E693", {"start": v(-662.83, -353.47) * mm, "end": v(-665.44, -350.11) * mm});
            skLineSegment(sketch, "E694", {"start": v(-658.69, -356.44) * mm, "end": v(-662.83, -353.47) * mm});
            skLineSegment(sketch, "E695", {"start": v(-652.82, -359.03) * mm, "end": v(-658.69, -356.44) * mm});
            skLineSegment(sketch, "E696", {"start": v(-645.17, -361.24) * mm, "end": v(-652.82, -359.03) * mm});
            skLineSegment(sketch, "E697", {"start": v(-635.88, -363.02) * mm, "end": v(-645.17, -361.24) * mm});
            skLineSegment(sketch, "E698", {"start": v(-625.41, -364.29) * mm, "end": v(-635.88, -363.02) * mm});
            skLineSegment(sketch, "E699", {"start": v(-614.36, -365.05) * mm, "end": v(-625.41, -364.29) * mm});
            skLineSegment(sketch, "E700", {"start": v(-603.36, -365.38) * mm, "end": v(-614.36, -365.05) * mm});
            skLineSegment(sketch, "E701", {"start": v(-592.82, -365.4) * mm, "end": v(-603.36, -365.38) * mm});
            skLineSegment(sketch, "E702", {"start": v(-583, -365.35) * mm, "end": v(-592.82, -365.4) * mm});
            skLineSegment(sketch, "E703", {"start": v(-573.85, -365.4) * mm, "end": v(-583, -365.35) * mm});
            skLineSegment(sketch, "E704", {"start": v(-565.37, -365.76) * mm, "end": v(-573.85, -365.4) * mm});
            skLineSegment(sketch, "E705", {"start": v(-557.57, -366.7) * mm, "end": v(-565.37, -365.76) * mm});
            skLineSegment(sketch, "E706", {"start": v(-550.6, -368.48) * mm, "end": v(-557.57, -366.7) * mm});
            skLineSegment(sketch, "E707", {"start": v(-544.82, -371.3) * mm, "end": v(-550.6, -368.48) * mm});
            skLineSegment(sketch, "E708", {"start": v(-540.63, -375.28) * mm, "end": v(-544.82, -371.3) * mm});
            skLineSegment(sketch, "E709", {"start": v(-538.31, -380.34) * mm, "end": v(-540.63, -375.28) * mm});
            skLineSegment(sketch, "E710", {"start": v(-537.9, -386.28) * mm, "end": v(-538.31, -380.34) * mm});
            skLineSegment(sketch, "E711", {"start": v(-539.28, -392.79) * mm, "end": v(-537.9, -386.28) * mm});
            skLineSegment(sketch, "E712", {"start": v(-542.05, -399.67) * mm, "end": v(-539.28, -392.79) * mm});
            skLineSegment(sketch, "E713", {"start": v(-545.88, -406.76) * mm, "end": v(-542.05, -399.67) * mm});
            skLineSegment(sketch, "E714", {"start": v(-550.48, -414.12) * mm, "end": v(-545.88, -406.76) * mm});
            skLineSegment(sketch, "E715", {"start": v(-555.64, -421.9) * mm, "end": v(-550.48, -414.12) * mm});
            skLineSegment(sketch, "E716", {"start": v(-561.25, -430.25) * mm, "end": v(-555.64, -421.9) * mm});
            skLineSegment(sketch, "E717", {"start": v(-567.1, -439.24) * mm, "end": v(-561.25, -430.25) * mm});
            skLineSegment(sketch, "E718", {"start": v(-572.86, -448.72) * mm, "end": v(-567.1, -439.24) * mm});
            skLineSegment(sketch, "E719", {"start": v(-578.14, -458.3) * mm, "end": v(-572.86, -448.72) * mm});
            skLineSegment(sketch, "E720", {"start": v(-582.59, -467.51) * mm, "end": v(-578.14, -458.3) * mm});
            skLineSegment(sketch, "E721", {"start": v(-585.89, -475.9) * mm, "end": v(-582.59, -467.51) * mm});
            skLineSegment(sketch, "E722", {"start": v(-587.87, -483.1) * mm, "end": v(-585.89, -475.9) * mm});
            skLineSegment(sketch, "E723", {"start": v(-588.58, -489.05) * mm, "end": v(-587.87, -483.1) * mm});
            skLineSegment(sketch, "E724", {"start": v(-588.02, -493.8) * mm, "end": v(-588.58, -489.05) * mm});
            skLineSegment(sketch, "E725", {"start": v(-586.3, -497.59) * mm, "end": v(-588.02, -493.8) * mm});
            skLineSegment(sketch, "E726", {"start": v(-583.25, -500.56) * mm, "end": v(-586.3, -497.59) * mm});
            skLineSegment(sketch, "E727", {"start": v(-578.78, -502.84) * mm, "end": v(-583.25, -500.56) * mm});
            skLineSegment(sketch, "E728", {"start": v(-572.68, -504.5) * mm, "end": v(-578.78, -502.84) * mm});
            skLineSegment(sketch, "E729", {"start": v(-564.88, -505.49) * mm, "end": v(-572.68, -504.5) * mm});
            skLineSegment(sketch, "E730", {"start": v(-555.54, -505.8) * mm, "end": v(-564.88, -505.49) * mm});
            skLineSegment(sketch, "E731", {"start": v(-545.07, -505.38) * mm, "end": v(-555.54, -505.8) * mm});
            skLineSegment(sketch, "E732", {"start": v(-534.1, -504.4) * mm, "end": v(-545.07, -505.38) * mm});
            skLineSegment(sketch, "E733", {"start": v(-523.15, -502.95) * mm, "end": v(-534.1, -504.4) * mm});
            skLineSegment(sketch, "E734", {"start": v(-512.69, -501.32) * mm, "end": v(-523.15, -502.95) * mm});
            skLineSegment(sketch, "E735", {"start": v(-502.93, -499.67) * mm, "end": v(-512.69, -501.32) * mm});
            skLineSegment(sketch, "E736", {"start": v(-493.84, -498.25) * mm, "end": v(-502.93, -499.67) * mm});
            skLineSegment(sketch, "E737", {"start": v(-485.36, -497.23) * mm, "end": v(-493.84, -498.25) * mm});
            skLineSegment(sketch, "E738", {"start": v(-477.46, -496.87) * mm, "end": v(-485.36, -497.23) * mm});
            skLineSegment(sketch, "E739", {"start": v(-470.24, -497.43) * mm, "end": v(-477.46, -496.87) * mm});
            skLineSegment(sketch, "E740", {"start": v(-464.02, -499.21) * mm, "end": v(-470.24, -497.43) * mm});
            skLineSegment(sketch, "E741", {"start": v(-459.17, -502.36) * mm, "end": v(-464.02, -499.21) * mm});
            skLineSegment(sketch, "E742", {"start": v(-455.94, -506.88) * mm, "end": v(-459.17, -502.36) * mm});
            skLineSegment(sketch, "E743", {"start": v(-454.5, -512.57) * mm, "end": v(-455.94, -506.88) * mm});
            skLineSegment(sketch, "E744", {"start": v(-454.7, -519.18) * mm, "end": v(-454.5, -512.57) * mm});
            skLineSegment(sketch, "E745", {"start": v(-456.25, -526.36) * mm, "end": v(-454.7, -519.18) * mm});
            skLineSegment(sketch, "E746", {"start": v(-458.84, -533.96) * mm, "end": v(-456.25, -526.36) * mm});
            skLineSegment(sketch, "E747", {"start": v(-462.17, -541.93) * mm, "end": v(-458.84, -533.96) * mm});
            skLineSegment(sketch, "E748", {"start": v(-466, -550.42) * mm, "end": v(-462.17, -541.93) * mm});
            skLineSegment(sketch, "E749", {"start": v(-470.2, -559.54) * mm, "end": v(-466, -550.42) * mm});
            skLineSegment(sketch, "E750", {"start": v(-474.54, -569.3) * mm, "end": v(-470.2, -559.54) * mm});
            skLineSegment(sketch, "E751", {"start": v(-478.75, -579.53) * mm, "end": v(-474.54, -569.3) * mm});
            skLineSegment(sketch, "E752", {"start": v(-482.51, -589.81) * mm, "end": v(-478.75, -579.53) * mm});
            skLineSegment(sketch, "E753", {"start": v(-485.5, -599.67) * mm, "end": v(-482.51, -589.81) * mm});
            skLineSegment(sketch, "E754", {"start": v(-487.51, -608.53) * mm, "end": v(-485.5, -599.67) * mm});
            skLineSegment(sketch, "E755", {"start": v(-488.43, -616.08) * mm, "end": v(-487.51, -608.53) * mm});
            skLineSegment(sketch, "E756", {"start": v(-488.28, -622.15) * mm, "end": v(-488.43, -616.08) * mm});
            skLineSegment(sketch, "E757", {"start": v(-487.06, -626.87) * mm, "end": v(-488.28, -622.15) * mm});
            skLineSegment(sketch, "E758", {"start": v(-484.8, -630.4) * mm, "end": v(-487.06, -626.87) * mm});
            skLineSegment(sketch, "E759", {"start": v(-481.42, -632.94) * mm, "end": v(-484.8, -630.4) * mm});
            skLineSegment(sketch, "E760", {"start": v(-476.72, -634.57) * mm, "end": v(-481.42, -632.94) * mm});
            skLineSegment(sketch, "E761", {"start": v(-470.52, -635.3) * mm, "end": v(-476.72, -634.57) * mm});
            skLineSegment(sketch, "E762", {"start": v(-462.78, -635.1) * mm, "end": v(-470.52, -635.3) * mm});
            skLineSegment(sketch, "E763", {"start": v(-453.6, -633.98) * mm, "end": v(-462.78, -635.1) * mm});
            skLineSegment(sketch, "E764", {"start": v(-443.42, -632) * mm, "end": v(-453.6, -633.98) * mm});
            skLineSegment(sketch, "E765", {"start": v(-432.75, -629.34) * mm, "end": v(-443.42, -632) * mm});
            skLineSegment(sketch, "E766", {"start": v(-422.14, -626.24) * mm, "end": v(-432.75, -629.34) * mm});
            skLineSegment(sketch, "E767", {"start": v(-412.03, -622.99) * mm, "end": v(-422.14, -626.24) * mm});
            skLineSegment(sketch, "E768", {"start": v(-402.58, -619.81) * mm, "end": v(-412.03, -622.99) * mm});
            skLineSegment(sketch, "E769", {"start": v(-393.76, -616.97) * mm, "end": v(-402.58, -619.81) * mm});
            skLineSegment(sketch, "E770", {"start": v(-385.48, -614.6) * mm, "end": v(-393.76, -616.97) * mm});
            skLineSegment(sketch, "E771", {"start": v(-377.69, -612.95) * mm, "end": v(-385.48, -614.6) * mm});
            skLineSegment(sketch, "E772", {"start": v(-370.45, -612.32) * mm, "end": v(-377.69, -612.95) * mm});
            skLineSegment(sketch, "E773", {"start": v(-363.97, -613) * mm, "end": v(-370.45, -612.32) * mm});
            skLineSegment(sketch, "E774", {"start": v(-358.6, -615.24) * mm, "end": v(-363.97, -613) * mm});
            skLineSegment(sketch, "E775", {"start": v(-354.65, -619.1) * mm, "end": v(-358.6, -615.24) * mm});
            skLineSegment(sketch, "E776", {"start": v(-352.2, -624.4) * mm, "end": v(-354.65, -619.1) * mm});
            skLineSegment(sketch, "E777", {"start": v(-351.3, -630.86) * mm, "end": v(-352.2, -624.4) * mm});
            skLineSegment(sketch, "E778", {"start": v(-351.62, -638.15) * mm, "end": v(-351.3, -630.86) * mm});
            skLineSegment(sketch, "E779", {"start": v(-352.95, -646.02) * mm, "end": v(-351.62, -638.15) * mm});
            skLineSegment(sketch, "E780", {"start": v(-354.95, -654.4) * mm, "end": v(-352.95, -646.02) * mm});
            skLineSegment(sketch, "E781", {"start": v(-357.4, -663.37) * mm, "end": v(-354.95, -654.4) * mm});
            skLineSegment(sketch, "E782", {"start": v(-360.13, -672.97) * mm, "end": v(-357.4, -663.37) * mm});
            skLineSegment(sketch, "E783", {"start": v(-362.93, -683.26) * mm, "end": v(-360.13, -672.97) * mm});
            skLineSegment(sketch, "E784", {"start": v(-365.54, -693.98) * mm, "end": v(-362.93, -683.26) * mm});
            skLineSegment(sketch, "E785", {"start": v(-367.7, -704.75) * mm, "end": v(-365.54, -693.98) * mm});
            skLineSegment(sketch, "E786", {"start": v(-369.2, -714.96) * mm, "end": v(-367.7, -704.75) * mm});
            skLineSegment(sketch, "E787", {"start": v(-369.91, -724.1) * mm, "end": v(-369.2, -714.96) * mm});
            skLineSegment(sketch, "E788", {"start": v(-369.74, -731.8) * mm, "end": v(-369.91, -724.1) * mm});
            skLineSegment(sketch, "E789", {"start": v(-368.7, -737.92) * mm, "end": v(-369.74, -731.8) * mm});
            skLineSegment(sketch, "E790", {"start": v(-366.81, -742.52) * mm, "end": v(-368.7, -737.92) * mm});
            skLineSegment(sketch, "E791", {"start": v(-364.1, -745.77) * mm, "end": v(-366.81, -742.52) * mm});
            skLineSegment(sketch, "E792", {"start": v(-360.41, -747.83) * mm, "end": v(-364.1, -745.77) * mm});
            skLineSegment(sketch, "E793", {"start": v(-355.59, -748.8) * mm, "end": v(-360.41, -747.83) * mm});
            skLineSegment(sketch, "E794", {"start": v(-349.47, -748.64) * mm, "end": v(-355.59, -748.8) * mm});
            skLineSegment(sketch, "E795", {"start": v(-341.92, -747.34) * mm, "end": v(-349.47, -748.64) * mm});
            skLineSegment(sketch, "E796", {"start": v(-333.13, -744.9) * mm, "end": v(-341.92, -747.34) * mm});
            skLineSegment(sketch, "E797", {"start": v(-323.43, -741.45) * mm, "end": v(-333.13, -744.9) * mm});
            skLineSegment(sketch, "E798", {"start": v(-313.32, -737.2) * mm, "end": v(-323.43, -741.45) * mm});
            skLineSegment(sketch, "E799", {"start": v(-303.29, -732.56) * mm, "end": v(-313.32, -737.2) * mm});
            skLineSegment(sketch, "E800", {"start": v(-293.76, -727.79) * mm, "end": v(-303.29, -732.56) * mm});
            skLineSegment(sketch, "E801", {"start": v(-284.82, -723.21) * mm, "end": v(-293.76, -727.79) * mm});
            skLineSegment(sketch, "E802", {"start": v(-276.5, -719.02) * mm, "end": v(-284.82, -723.21) * mm});
            skLineSegment(sketch, "E803", {"start": v(-268.62, -715.4) * mm, "end": v(-276.5, -719.02) * mm});
            skLineSegment(sketch, "E804", {"start": v(-261.12, -712.52) * mm, "end": v(-268.62, -715.4) * mm});
            skLineSegment(sketch, "E805", {"start": v(-254.04, -710.72) * mm, "end": v(-261.12, -712.52) * mm});
            skLineSegment(sketch, "E806", {"start": v(-247.51, -710.31) * mm, "end": v(-254.04, -710.72) * mm});
            skLineSegment(sketch, "E807", {"start": v(-241.82, -711.6) * mm, "end": v(-247.51, -710.31) * mm});
            skLineSegment(sketch, "E808", {"start": v(-237.25, -714.65) * mm, "end": v(-241.82, -711.6) * mm});
            skLineSegment(sketch, "E809", {"start": v(-233.95, -719.4) * mm, "end": v(-237.25, -714.65) * mm});
            skLineSegment(sketch, "E810", {"start": v(-231.97, -725.58) * mm, "end": v(-233.95, -719.4) * mm});
            skLineSegment(sketch, "E811", {"start": v(-231.13, -732.76) * mm, "end": v(-231.97, -725.58) * mm});
            skLineSegment(sketch, "E812", {"start": v(-231.18, -740.71) * mm, "end": v(-231.13, -732.76) * mm});
            skLineSegment(sketch, "E813", {"start": v(-231.84, -749.27) * mm, "end": v(-231.18, -740.71) * mm});
            skLineSegment(sketch, "E814", {"start": v(-232.9, -758.47) * mm, "end": v(-231.84, -749.27) * mm});
            skLineSegment(sketch, "E815", {"start": v(-234.15, -768.35) * mm, "end": v(-232.9, -758.47) * mm});
            skLineSegment(sketch, "E816", {"start": v(-235.37, -778.9) * mm, "end": v(-234.15, -768.35) * mm});
            skLineSegment(sketch, "E817", {"start": v(-236.39, -789.86) * mm, "end": v(-235.37, -778.9) * mm});
            skLineSegment(sketch, "E818", {"start": v(-236.94, -800.84) * mm, "end": v(-236.39, -789.86) * mm});
            skLineSegment(sketch, "E819", {"start": v(-236.97, -811.2) * mm, "end": v(-236.94, -800.84) * mm});
            skLineSegment(sketch, "E820", {"start": v(-236.33, -820.45) * mm, "end": v(-236.97, -811.2) * mm});
            skLineSegment(sketch, "E821", {"start": v(-235.04, -828.14) * mm, "end": v(-236.33, -820.45) * mm});
            skLineSegment(sketch, "E822", {"start": v(-233.16, -834.16) * mm, "end": v(-235.04, -828.14) * mm});
            skLineSegment(sketch, "E823", {"start": v(-230.67, -838.53) * mm, "end": v(-233.16, -834.16) * mm});
            skLineSegment(sketch, "E824", {"start": v(-227.52, -841.45) * mm, "end": v(-230.67, -838.53) * mm});
            skLineSegment(sketch, "E825", {"start": v(-223.6, -843.03) * mm, "end": v(-227.52, -841.45) * mm});
            skLineSegment(sketch, "E826", {"start": v(-218.76, -843.36) * mm, "end": v(-223.6, -843.03) * mm});
            skLineSegment(sketch, "E827", {"start": v(-212.79, -842.4) * mm, "end": v(-218.76, -843.36) * mm});
            skLineSegment(sketch, "E828", {"start": v(-205.63, -840.05) * mm, "end": v(-212.79, -842.4) * mm});
            skLineSegment(sketch, "E829", {"start": v(-197.37, -836.42) * mm, "end": v(-205.63, -840.05) * mm});
            skLineSegment(sketch, "E830", {"start": v(-188.33, -831.62) * mm, "end": v(-197.37, -836.42) * mm});
            skLineSegment(sketch, "E831", {"start": v(-178.98, -825.98) * mm, "end": v(-188.33, -831.62) * mm});
            skLineSegment(sketch, "E832", {"start": v(-169.76, -819.91) * mm, "end": v(-178.98, -825.98) * mm});
            skLineSegment(sketch, "E833", {"start": v(-161, -813.77) * mm, "end": v(-169.76, -819.91) * mm});
            skLineSegment(sketch, "E834", {"start": v(-152.8, -807.9) * mm, "end": v(-161, -813.77) * mm});
            skLineSegment(sketch, "E835", {"start": v(-145.12, -802.46) * mm, "end": v(-152.8, -807.9) * mm});
            skLineSegment(sketch, "E836", {"start": v(-137.83, -797.66) * mm, "end": v(-145.12, -802.46) * mm});
            skLineSegment(sketch, "E837", {"start": v(-130.82, -793.67) * mm, "end": v(-137.83, -797.66) * mm});
            skLineSegment(sketch, "E838", {"start": v(-124.04, -790.75) * mm, "end": v(-130.82, -793.67) * mm});
            skLineSegment(sketch, "E839", {"start": v(-117.64, -789.28) * mm, "end": v(-124.04, -790.75) * mm});
            skLineSegment(sketch, "E840", {"start": v(-111.77, -789.58) * mm, "end": v(-117.64, -789.28) * mm});
            skLineSegment(sketch, "E841", {"start": v(-106.74, -791.8) * mm, "end": v(-111.77, -789.58) * mm});
            skLineSegment(sketch, "E842", {"start": v(-102.73, -795.88) * mm, "end": v(-106.74, -791.8) * mm});
            skLineSegment(sketch, "E843", {"start": v(-99.8, -801.55) * mm, "end": v(-102.73, -795.88) * mm});
            skLineSegment(sketch, "E844", {"start": v(-97.85, -808.46) * mm, "end": v(-99.8, -801.55) * mm});
            skLineSegment(sketch, "E845", {"start": v(-96.66, -816.28) * mm, "end": v(-97.85, -808.46) * mm});
            skLineSegment(sketch, "E846", {"start": v(-96.02, -824.81) * mm, "end": v(-96.66, -816.28) * mm});
            skLineSegment(sketch, "E847", {"start": v(-95.72, -834.03) * mm, "end": v(-96.02, -824.81) * mm});
            skLineSegment(sketch, "E848", {"start": v(-95.5, -843.97) * mm, "end": v(-95.72, -834.03) * mm});
            skLineSegment(sketch, "E849", {"start": v(-95.16, -854.53) * mm, "end": v(-95.5, -843.97) * mm});
            skLineSegment(sketch, "E850", {"start": v(-94.58, -865.5) * mm, "end": v(-95.16, -854.53) * mm});
            skLineSegment(sketch, "E851", {"start": v(-93.59, -876.45) * mm, "end": v(-94.58, -865.5) * mm});
            skLineSegment(sketch, "E852", {"start": v(-92.11, -886.76) * mm, "end": v(-93.59, -876.45) * mm});
            skLineSegment(sketch, "E853", {"start": v(-90.18, -895.9) * mm, "end": v(-92.11, -886.76) * mm});
            skLineSegment(sketch, "E854", {"start": v(-87.82, -903.45) * mm, "end": v(-90.18, -895.9) * mm});
            skLineSegment(sketch, "E855", {"start": v(-85.1, -909.27) * mm, "end": v(-87.82, -903.45) * mm});
            skLineSegment(sketch, "E856", {"start": v(-82.03, -913.36) * mm, "end": v(-85.1, -909.27) * mm});
            skLineSegment(sketch, "E857", {"start": v(-78.5, -915.9) * mm, "end": v(-82.03, -913.36) * mm});
            skLineSegment(sketch, "E858", {"start": v(-74.43, -917) * mm, "end": v(-78.5, -915.9) * mm});
            skLineSegment(sketch, "E859", {"start": v(-69.63, -916.71) * mm, "end": v(-74.43, -917) * mm});
            skLineSegment(sketch, "E860", {"start": v(-63.92, -914.96) * mm, "end": v(-69.63, -916.71) * mm});
            skLineSegment(sketch, "E861", {"start": v(-57.24, -911.73) * mm, "end": v(-63.92, -914.96) * mm});
            skLineSegment(sketch, "E862", {"start": v(-49.67, -907.03) * mm, "end": v(-57.24, -911.73) * mm});
            skLineSegment(sketch, "E863", {"start": v(-41.47, -901.04) * mm, "end": v(-49.67, -907.03) * mm});
            skLineSegment(sketch, "E864", {"start": v(-33.06, -894.16) * mm, "end": v(-41.47, -901.04) * mm});
            skLineSegment(sketch, "E865", {"start": v(-24.8, -886.84) * mm, "end": v(-33.06, -894.16) * mm});
            skLineSegment(sketch, "E866", {"start": v(-16.98, -879.48) * mm, "end": v(-24.8, -886.84) * mm});
            skLineSegment(sketch, "E867", {"start": v(-9.66, -872.44) * mm, "end": v(-16.98, -879.48) * mm});
            skLineSegment(sketch, "E868", {"start": v(-2.8, -865.91) * mm, "end": v(-9.66, -872.44) * mm});
            skLineSegment(sketch, "E869", {"start": v(3.72, -860.04) * mm, "end": v(-2.8, -865.91) * mm});
            skFitSpline(sketch, "E870", {"points": [v(18.1, -843.84) * mm, v(13.66, -850) * mm, v(8.8, -855.49) * mm, v(3.72, -860.04) * mm]});
            skFitSpline(sketch, "E871", {"points": [v(112.5, -344.18) * mm, v(120.54, -417.8) * mm, v(119.3, -533.27) * mm, v(91.94, -737.4) * mm, v(18.48, -843.31) * mm, v(18.1, -843.84) * mm]});
            skLineSegment(sketch, "E872", {"start": v(112.5, -344.18) * mm, "end": v(93.37, -169.04) * mm});
            skFitSpline(sketch, "E873", {"points": [v(93.37, -169.04) * mm, v(93.54, -169.12) * mm, v(93.72, -169.2) * mm, v(93.9, -169.27) * mm, v(94.07, -169.34) * mm]});
            skFitSpline(sketch, "E874", {"points": [v(197.75, -241.15) * mm, v(183.73, -226.38) * mm, v(166.44, -198.36) * mm, v(124.43, -182.9) * mm, v(94.07, -169.34) * mm]});
            skLineSegment(sketch, "E875", {"start": v(202.1, -245.72) * mm, "end": v(197.75, -241.15) * mm});
            skLineSegment(sketch, "E876", {"start": v(205.7, -248.34) * mm, "end": v(202.1, -245.72) * mm});
            skLineSegment(sketch, "E877", {"start": v(208.8, -249.56) * mm, "end": v(205.7, -248.34) * mm});
            skLineSegment(sketch, "E878", {"start": v(211.82, -249.66) * mm, "end": v(208.8, -249.56) * mm});
            skLineSegment(sketch, "E879", {"start": v(215.23, -248.64) * mm, "end": v(211.82, -249.66) * mm});
            skLineSegment(sketch, "E880", {"start": v(219.5, -246.2) * mm, "end": v(215.23, -248.64) * mm});
            skLineSegment(sketch, "E881", {"start": v(224.88, -241.83) * mm, "end": v(219.5, -246.2) * mm});
            skLineSegment(sketch, "E882", {"start": v(231.25, -235.33) * mm, "end": v(224.88, -241.83) * mm});
            skLineSegment(sketch, "E883", {"start": v(238.19, -226.8) * mm, "end": v(231.25, -235.33) * mm});
            skLineSegment(sketch, "E884", {"start": v(244.94, -216.94) * mm, "end": v(238.19, -226.8) * mm});
            skLineSegment(sketch, "E885", {"start": v(250.89, -206.65) * mm, "end": v(244.94, -216.94) * mm});
            skLineSegment(sketch, "E886", {"start": v(255.71, -196.85) * mm, "end": v(250.89, -206.65) * mm});
            skLineSegment(sketch, "E887", {"start": v(259.52, -188.01) * mm, "end": v(255.71, -196.85) * mm});
            skLineSegment(sketch, "E888", {"start": v(265.5, -172.77) * mm, "end": v(259.52, -188.01) * mm});
            skLineSegment(sketch, "E889", {"start": v(268.57, -165.79) * mm, "end": v(265.5, -172.77) * mm});
            skLineSegment(sketch, "E890", {"start": v(272.28, -159.13) * mm, "end": v(268.57, -165.79) * mm});
            skLineSegment(sketch, "E891", {"start": v(276.9, -153.34) * mm, "end": v(272.28, -159.13) * mm});
            skLineSegment(sketch, "E892", {"start": v(282.54, -149.2) * mm, "end": v(276.9, -153.34) * mm});
            skLineSegment(sketch, "E893", {"start": v(288.91, -147.42) * mm, "end": v(282.54, -149.2) * mm});
            skLineSegment(sketch, "E894", {"start": v(295.54, -148.34) * mm, "end": v(288.91, -147.42) * mm});
            skLineSegment(sketch, "E895", {"start": v(301.84, -151.64) * mm, "end": v(295.54, -148.34) * mm});
            skLineSegment(sketch, "E896", {"start": v(307.48, -156.57) * mm, "end": v(301.84, -151.64) * mm});
            skLineSegment(sketch, "E897", {"start": v(312.43, -162.38) * mm, "end": v(307.48, -156.57) * mm});
            skLineSegment(sketch, "E898", {"start": v(316.88, -168.6) * mm, "end": v(312.43, -162.38) * mm});
            skLineSegment(sketch, "E899", {"start": v(321.32, -175.18) * mm, "end": v(316.88, -168.6) * mm});
            skLineSegment(sketch, "E900", {"start": v(326.25, -182.37) * mm, "end": v(321.32, -175.18) * mm});
            skLineSegment(sketch, "E901", {"start": v(332.17, -190.35) * mm, "end": v(326.25, -182.37) * mm});
            skLineSegment(sketch, "E902", {"start": v(339.3, -198.96) * mm, "end": v(332.17, -190.35) * mm});
            skLineSegment(sketch, "E903", {"start": v(347.48, -207.6) * mm, "end": v(339.3, -198.96) * mm});
            skFitSpline(sketch, "E904", {"points": [v(68.11, -347.2) * mm, v(68.3, -348.86) * mm, v(70.12, -365.71) * mm, v(73.94, -412.68) * mm, v(74.38, -472.12) * mm, v(70.88, -534.67) * mm, v(66.54, -584.4) * mm, v(59.89, -634.42) * mm, v(49.1, -683.3) * mm, v(32.4, -729.43) * mm, v(13.1, -766.94) * mm, v(1.47, -787) * mm, v(-2.67, -793.86) * mm, v(-3.59, -795.37) * mm]});
            skFitSpline(sketch, "E905", {"points": [v(-24.4, -787.1) * mm, v(-17.5, -789.93) * mm, v(-10.56, -792.7) * mm, v(-3.59, -795.37) * mm]});
            skFitSpline(sketch, "E906", {"points": [v(-24.4, -787.1) * mm, v(-30.55, -784.57) * mm, v(-36.67, -781.99) * mm, v(-42.76, -779.35) * mm]});
            skArc(sketch, "E907", {"start": v(-43.59, -779) * mm, "mid": v(-43.18, -779.18) * mm, "end": v(-42.76, -779.35) * mm});
            skFitSpline(sketch, "E908", {"points": [v(-70.14, -766.99) * mm, v(-67.4, -768.27) * mm, v(-58.6, -772.36) * mm, v(-49.73, -776.33) * mm, v(-43.59, -779) * mm]});
            skFitSpline(sketch, "E909", {"points": [v(-188.27, -701.38) * mm, v(-157.72, -721.2) * mm, v(-126.08, -739.31) * mm, v(-85.79, -759.52) * mm, v(-77.99, -763.3) * mm, v(-70.14, -766.99) * mm]});
            skFitSpline(sketch, "E910", {"points": [v(-223.12, -677.7) * mm, v(-211.68, -685.84) * mm, v(-200.05, -693.74) * mm, v(-188.27, -701.38) * mm]});
            skFitSpline(sketch, "E911", {"points": [v(-312.98, -605.37) * mm, v(-303.04, -614.4) * mm, v(-274.04, -639.68) * mm, v(-243.54, -663.18) * mm, v(-223.12, -677.7) * mm]});
            skFitSpline(sketch, "E912", {"points": [v(-336.9, -582.87) * mm, v(-329.07, -590.5) * mm, v(-321.11, -597.98) * mm, v(-313.03, -605.32) * mm]});
            skFitSpline(sketch, "E913", {"points": [v(-367.53, -551.6) * mm, v(-358.97, -560.77) * mm, v(-350.22, -569.75) * mm, v(-339.83, -580) * mm, v(-338.36, -581.44) * mm, v(-336.9, -582.87) * mm]});
            skFitSpline(sketch, "E914", {"points": [v(-393.7, -522.4) * mm, v(-385.18, -532.32) * mm, v(-376.46, -542.06) * mm, v(-367.53, -551.6) * mm]});
            skFitSpline(sketch, "E915", {"points": [v(-542.4, -282.57) * mm, v(-519.88, -336.26) * mm, v(-474.78, -419.67) * mm, v(-417.27, -494.99) * mm, v(-393.7, -522.4) * mm]});
            skFitSpline(sketch, "E916", {"points": [v(-105.43, 44.86) * mm, v(-127.7, 63.42) * mm, v(-183.98, 69.8) * mm, v(-271.32, 65.7) * mm, v(-357.1, 29.91) * mm, v(-436.87, -44.16) * mm, v(-502.92, -142.27) * mm, v(-531.3, -230.18) * mm, v(-541.4, -277.54) * mm, v(-542.4, -282.57) * mm]});
            skFitSpline(sketch, "E917", {"points": [v(-105.43, 44.86) * mm, v(-105.43, 44.86) * mm, v(-105.43, 44.86) * mm, v(-105.43, 44.86) * mm]});
            skLineSegment(sketch, "E918", {"start": v(-105.42, 44.87) * mm, "end": v(-105.43, 44.86) * mm});
            skFitSpline(sketch, "E919", {"points": [v(-105.42, 44.87) * mm, v(-104.9, 43.22) * mm, v(-104.35, 41.58) * mm, v(-103.8, 39.94) * mm, v(-103.23, 38.3) * mm]});
            skFitSpline(sketch, "E920", {"points": [v(-103.23, 38.3) * mm, v(-103.23, 38.3) * mm, v(-103.23, 38.3) * mm, v(-103.23, 38.3) * mm]});
            skFitSpline(sketch, "E921", {"points": [v(-103.2, 38.18) * mm, v(-103.2, 38.22) * mm, v(-103.22, 38.26) * mm, v(-103.23, 38.3) * mm]});
            skFitSpline(sketch, "E922", {"points": [v(-103.2, 38.18) * mm, v(-102.06, 34.9) * mm, v(-91.24, 5.01) * mm, v(-73, -30.45) * mm, v(-49.47, -62.67) * mm, v(-24.42, -88.7) * mm, v(-18.85, -94.16) * mm]});
            skFitSpline(sketch, "E923", {"points": [v(-18.85, -94.16) * mm, v(-18.72, -94.28) * mm, v(-18.6, -94.4) * mm, v(-18.47, -94.53) * mm]});
            skFitSpline(sketch, "E924", {"points": [v(-18.47, -94.53) * mm, v(-10.4, -102.4) * mm, v(-1.97, -109.9) * mm, v(6.84, -117.02) * mm]});
            skFitSpline(sketch, "E925", {"points": [v(6.84, -117.02) * mm, v(6.95, -117.1) * mm, v(7.06, -117.19) * mm, v(7.16, -117.28) * mm]});
            skFitSpline(sketch, "E926", {"points": [v(7.16, -117.28) * mm, v(16.37, -124.7) * mm, v(25.94, -131.74) * mm, v(35.8, -138.36) * mm, v(45.94, -144.55) * mm, v(45.98, -144.57) * mm]});
            skLineSegment(sketch, "E927", {"start": v(68.11, -347.2) * mm, "end": v(45.98, -144.57) * mm});
            skFitSpline(sketch, "E928", {"points": [v(-531.75, 386.03) * mm, v(-543.22, 362.39) * mm, v(-580.27, 274.65) * mm, v(-600.52, 180.54) * mm, v(-606.26, 111.56) * mm]});
            skFitSpline(sketch, "E929", {"points": [v(-66.85, 314.55) * mm, v(-72.53, 332.97) * mm, v(-93.2, 359.83) * mm, v(-123.9, 391.85) * mm, v(-164.67, 420.3) * mm, v(-211.8, 444.6) * mm, v(-274.5, 454.08) * mm, v(-330.42, 453.94) * mm, v(-386.2, 445.78) * mm, v(-432.5, 434.49) * mm, v(-480.58, 413.12) * mm, v(-512.7, 397.69) * mm, v(-531.75, 386.03) * mm]});
            skFitSpline(sketch, "E930", {"points": [v(-111.95, 216.32) * mm, v(-111.94, 216.35) * mm, v(-107.2, 235.38) * mm, v(-94.96, 269.68) * mm, v(-76.54, 301.01) * mm, v(-66.85, 314.55) * mm]});
            skFitSpline(sketch, "E931", {"points": [v(-606.26, 111.56) * mm, v(-599.07, 121.33) * mm, v(-582.57, 142.1) * mm, v(-555.07, 170.43) * mm, v(-525.7, 198.5) * mm, v(-492.22, 225.38) * mm, v(-455.45, 246.89) * mm, v(-419.2, 264.68) * mm, v(-379.62, 281.56) * mm, v(-335.01, 290.25) * mm, v(-291.51, 290.67) * mm, v(-234.68, 283.61) * mm, v(-179.53, 265.85) * mm, v(-135.2, 238.02) * mm, v(-117.7, 222.21) * mm, v(-111.95, 216.32) * mm]});
            skFitSpline(sketch, "E932", {"points": [v(-58.52, 765.28) * mm, v(-120.93, 752.28) * mm, v(-202.85, 721.83) * mm, v(-276.77, 676.21) * mm, v(-295.33, 663.44) * mm]});
            skFitSpline(sketch, "E933", {"points": [v(139.77, 425.35) * mm, v(145.4, 456.93) * mm, v(144.27, 499.82) * mm, v(135.03, 553.29) * mm, v(126.67, 585.7) * mm, v(112.97, 617.6) * mm, v(89.58, 655.58) * mm, v(52.76, 692.88) * mm, v(6.3, 732.53) * mm, v(-32.27, 752.98) * mm, v(-54.65, 763.51) * mm, v(-58.52, 765.28) * mm]});
            skFitSpline(sketch, "E934", {"points": [v(54.4, 409.09) * mm, v(56.36, 409.84) * mm, v(82.37, 419.37) * mm, v(111.39, 424.85) * mm, v(138.37, 425.34) * mm, v(139.77, 425.35) * mm]});
            skFitSpline(sketch, "E935", {"points": [v(-295.33, 663.44) * mm, v(-294.1, 663.43) * mm, v(-282.47, 663.3) * mm, v(-259.36, 663.05) * mm, v(-225.46, 659.69) * mm, v(-192.78, 653.37) * mm, v(-149.92, 642.27) * mm, v(-96.6, 620.93) * mm, v(-40.48, 581.17) * mm, v(6.77, 530.79) * mm, v(38.93, 470.69) * mm, v(50.45, 429.2) * mm, v(54.4, 409.09) * mm]});
            skFitSpline(sketch, "E936", {"points": [v(238.61, 752.78) * mm, v(242.3, 747.6) * mm, v(251.26, 734.68) * mm, v(268.41, 703.05) * mm, v(280.8, 669) * mm, v(291.18, 635.7) * mm, v(298.4, 608.84) * mm, v(302.64, 580.45) * mm, v(304.21, 542.8) * mm, v(299.49, 495.9) * mm, v(284.9, 441.62) * mm, v(270.75, 408.38) * mm, v(262.54, 392.17) * mm]});
            skFitSpline(sketch, "E937", {"points": [v(402.74, 670.87) * mm, v(356.99, 704.3) * mm, v(301.66, 732.7) * mm, v(242.91, 751.46) * mm, v(238.61, 752.78) * mm]});
            skFitSpline(sketch, "E938", {"points": [v(315.76, 343.8) * mm, v(331.66, 356.3) * mm, v(349.7, 385.4) * mm, v(379.23, 425.33) * mm, v(394.2, 461.68) * mm, v(405.46, 487.47) * mm, v(409.92, 514.5) * mm, v(412.98, 532.58) * mm, v(412.72, 581.3) * mm, v(413.55, 624.1) * mm, v(405.94, 658.61) * mm, v(402.74, 670.87) * mm]});
            skFitSpline(sketch, "E939", {"points": [v(250.81, 398.12) * mm, v(251.87, 397.54) * mm, v(276.66, 383.81) * mm, v(298.8, 365.16) * mm, v(315.73, 343.84) * mm, v(315.76, 343.8) * mm]});
            skLineSegment(sketch, "E940", {"start": v(262.54, 392.17) * mm, "end": v(250.81, 398.12) * mm});
            skFitSpline(sketch, "E941", {"points": [v(567.57, 468.16) * mm, v(565.49, 460.02) * mm, v(558.73, 436.65) * mm, v(544.41, 399.1) * mm, v(520.64, 354.72) * mm, v(485.43, 317.16) * mm, v(445.44, 288.9) * mm, v(411.1, 269.36) * mm, v(384.57, 254.86) * mm, v(372.3, 248.02) * mm, v(366.1, 244.43) * mm]});
            skFitSpline(sketch, "E942", {"points": [v(605.67, 322.66) * mm, v(602.87, 353.12) * mm, v(593.23, 402.75) * mm, v(575.58, 450.15) * mm, v(567.57, 468.16) * mm]});
            skFitSpline(sketch, "E943", {"points": [v(355, 189.84) * mm, v(377.67, 193.32) * mm, v(420.08, 199.9) * mm, v(480.46, 212.9) * mm, v(532.62, 240.59) * mm, v(574.57, 277.73) * mm, v(596.56, 307.97) * mm, v(605.67, 322.66) * mm]});
            skLineSegment(sketch, "E944", {"start": v(354.97, 189.84) * mm, "end": v(355, 189.84) * mm});
            skFitSpline(sketch, "E945", {"points": [v(357.56, 239.82) * mm, v(358.97, 223.12) * mm, v(358.13, 206.23) * mm, v(354.97, 189.84) * mm]});
            skLineSegment(sketch, "E946", {"start": v(366.1, 244.43) * mm, "end": v(357.56, 239.82) * mm});
            skFitSpline(sketch, "E947", {"points": [v(560.61, 87.22) * mm, v(552.6, 83.74) * mm, v(531.19, 75.18) * mm, v(498.93, 66.22) * mm, v(465.53, 66.03) * mm, v(443.3, 69.02) * mm, v(421.94, 73.1) * mm, v(400.91, 78.45) * mm, v(380.6, 84.67) * mm, v(361.13, 91.04) * mm, v(340.4, 98.53) * mm, v(325.63, 105.93) * mm, v(318.82, 110.13) * mm]});
            skFitSpline(sketch, "E948", {"points": [v(484.18, -14.74) * mm, v(514.87, 14.46) * mm, v(540.7, 49.14) * mm, v(560.61, 87.22) * mm]});
            skFitSpline(sketch, "E949", {"points": [v(289.36, 86.16) * mm, v(302.09, 72.59) * mm, v(326.36, 50.66) * mm, v(360.39, 22.83) * mm, v(385.92, 4.41) * mm, v(420.9, -13.32) * mm, v(453.87, -15.7) * mm, v(479.93, -14.94) * mm, v(484.18, -14.74) * mm]});
            skLineSegment(sketch, "E950", {"start": v(289.35, 86.17) * mm, "end": v(289.36, 86.16) * mm});
            skFitSpline(sketch, "E951", {"points": [v(316.98, 111.27) * mm, v(308.79, 101.88) * mm, v(299.5, 93.42) * mm, v(289.35, 86.17) * mm]});
            skLineSegment(sketch, "E952", {"start": v(318.82, 110.13) * mm, "end": v(316.98, 111.27) * mm});
            skFitSpline(sketch, "E953", {"points": [v(322.11, -103.04) * mm, v(318.85, -100.75) * mm, v(307.03, -91.9) * mm, v(288.46, -74.37) * mm, v(269.25, -49.4) * mm, v(253.74, -24.39) * mm, v(239.5, -0.1) * mm, v(225.58, 24.78) * mm, v(216.62, 42.82) * mm, v(212.66, 51.92) * mm]});
            skLineSegment(sketch, "E954", {"start": v(322.11, -103.04) * mm, "end": v(333.52, -111.06) * mm});
            skFitSpline(sketch, "E955", {"points": [v(333.52, -111.06) * mm, v(302.27, -122.07) * mm, v(269.32, -128.37) * mm, v(235.1, -128.7) * mm, v(234.87, -128.7) * mm]});
            skLineSegment(sketch, "E956", {"start": v(234.87, -128.7) * mm, "end": v(224.53, -110.7) * mm});
            skFitSpline(sketch, "E957", {"points": [v(189.3, 59.26) * mm, v(184.93, 54) * mm, v(183.8, 46.16) * mm, v(183.83, 21.86) * mm, v(185.73, 1.1) * mm, v(192.65, -52.1) * mm, v(205.22, -78.7) * mm, v(219.12, -102.5) * mm, v(224.53, -110.7) * mm]});
            skLineSegment(sketch, "E958", {"start": v(189.3, 59.27) * mm, "end": v(189.3, 59.26) * mm});
            skFitSpline(sketch, "E959", {"points": [v(209.77, 58.57) * mm, v(203.2, 58.3) * mm, v(196.35, 58.5) * mm, v(189.55, 59.24) * mm, v(189.3, 59.27) * mm]});
            skLineSegment(sketch, "E960", {"start": v(212.66, 51.92) * mm, "end": v(209.77, 58.57) * mm});
            skFitSpline(sketch, "E961", {"points": [v(54.89, 200.27) * mm, v(42.2, 200.66) * mm, v(20.03, 201.04) * mm, v(-10.14, 191.04) * mm, v(-39.88, 170.99) * mm, v(-59.75, 153.16) * mm, v(-70.08, 139.44) * mm]});
            skArc(sketch, "E962", {"start": v(54.89, 200.27) * mm, "mid": v(54.99, 186.1) * mm, "end": v(56.67, 172.04) * mm});
            skFitSpline(sketch, "E963", {"points": [v(-58.94, 66.43) * mm, v(-55.06, 75.04) * mm, v(-44.89, 93.46) * mm, v(-24.26, 118.7) * mm, v(-4.5, 137.04) * mm, v(14, 150.96) * mm, v(34.5, 162.72) * mm, v(48.49, 168.36) * mm, v(56.67, 172.04) * mm]});
            skFitSpline(sketch, "E964", {"points": [v(-70.08, 139.44) * mm, v(-69.77, 114.75) * mm, v(-65.98, 90.1) * mm, v(-58.94, 66.43) * mm]});
            skFitSpline(sketch, "E965", {"points": [v(453.94, -40.51) * mm, v(454.03, -40.44) * mm, v(454.13, -40.36) * mm, v(454.22, -40.3) * mm]});
            skLineSegment(sketch, "E966", {"start": v(453.94, -40.51) * mm, "end": v(455.23, -40.4) * mm});
            skFitSpline(sketch, "E967", {"points": [v(455.23, -40.4) * mm, v(426.88, -63.72) * mm, v(396.53, -83.53) * mm, v(364.46, -98.44) * mm]});
            skLineSegment(sketch, "E968", {"start": v(364.46, -98.44) * mm, "end": v(355.15, -93.54) * mm});
            skFitSpline(sketch, "E969", {"points": [v(235.95, 62.06) * mm, v(240.8, 50.92) * mm, v(252.57, 28.1) * mm, v(275.35, -11.23) * mm, v(303.96, -57.53) * mm, v(336.66, -83.81) * mm, v(355.15, -93.54) * mm]});
            skLineSegment(sketch, "E970", {"start": v(235.94, 62.08) * mm, "end": v(235.95, 62.06) * mm});
            skFitSpline(sketch, "E971", {"points": [v(266.95, 72.92) * mm, v(257.07, 68.18) * mm, v(246.64, 64.53) * mm, v(235.94, 62.08) * mm]});
            skLineSegment(sketch, "E972", {"start": v(270.84, 68.78) * mm, "end": v(266.95, 72.92) * mm});
            skFitSpline(sketch, "E973", {"points": [v(454.22, -40.3) * mm, v(447.4, -40.01) * mm, v(429, -38.55) * mm, v(397.55, -31.19) * mm, v(366.08, -13.06) * mm, v(341, 5.99) * mm, v(316.93, 25.62) * mm, v(293.6, 45.95) * mm, v(278.13, 61) * mm, v(270.84, 68.78) * mm]});
            skFitSpline(sketch, "E974", {"points": [v(607.57, 280.8) * mm, v(603.22, 275.15) * mm, v(579.74, 246.7) * mm, v(538.98, 213.19) * mm, v(482.83, 188.15) * mm, v(425.62, 174.76) * mm, v(386.06, 168.9) * mm, v(358.84, 164.73) * mm]});
            skFitSpline(sketch, "E975", {"points": [v(577.16, 122.95) * mm, v(583.99, 139.76) * mm, v(600.9, 190.86) * mm, v(607.53, 244.87) * mm, v(607.57, 280.8) * mm]});
            skFitSpline(sketch, "E976", {"points": [v(332.18, 131.74) * mm, v(346.2, 123.08) * mm, v(373.4, 113.6) * mm, v(412.77, 101.1) * mm, v(447.54, 93.63) * mm, v(485.05, 89.83) * mm, v(522.25, 98.5) * mm, v(553.3, 111.61) * mm, v(571.03, 119.88) * mm, v(577.16, 122.95) * mm]});
            skFitSpline(sketch, "E977", {"points": [v(347.5, 163) * mm, v(343.5, 152.08) * mm, v(338.36, 141.59) * mm, v(332.18, 131.74) * mm]});
            skLineSegment(sketch, "E978", {"start": v(358.84, 164.73) * mm, "end": v(347.5, 163) * mm});
            skFitSpline(sketch, "E979", {"points": [v(434.15, 646.05) * mm, v(434.3, 645.18) * mm, v(437.29, 626.26) * mm, v(438.38, 597.18) * mm, v(438.22, 562.53) * mm, v(438.26, 534.71) * mm, v(435.85, 515.75) * mm, v(433.82, 503.3) * mm, v(432.7, 496.43) * mm, v(431.13, 487.5) * mm, v(427.66, 475.6) * mm, v(422.92, 463.86) * mm, v(418.52, 453.66) * mm, v(412.61, 439.75) * mm, v(404.48, 421.58) * mm, v(391.53, 399.58) * mm, v(378.15, 380.89) * mm, v(366.3, 363.22) * mm, v(354.26, 346.33) * mm, v(342.35, 333.18) * mm, v(335.16, 326.75) * mm, v(331.45, 323.83) * mm]});
            skFitSpline(sketch, "E980", {"points": [v(549.36, 504.86) * mm, v(526.15, 547.1) * mm, v(488.94, 596.33) * mm, v(443.78, 637.83) * mm, v(434.15, 646.05) * mm]});
            skFitSpline(sketch, "E981", {"points": [v(353.4, 266.42) * mm, v(400.67, 293.75) * mm, v(481.04, 329.79) * mm, v(530.6, 428.23) * mm, v(544.87, 477.66) * mm, v(549.36, 504.86) * mm]});
            skLineSegment(sketch, "E982", {"start": v(353.39, 266.42) * mm, "end": v(353.4, 266.42) * mm});
            skFitSpline(sketch, "E983", {"points": [v(330.34, 322.82) * mm, v(340.42, 306.16) * mm, v(348.43, 287.18) * mm, v(353.18, 267.31) * mm, v(353.39, 266.42) * mm]});
            skLineSegment(sketch, "E984", {"start": v(331.45, 323.83) * mm, "end": v(330.34, 322.82) * mm});
            skFitSpline(sketch, "E985", {"points": [v(199.58, 763.23) * mm, v(135.62, 777.95) * mm, v(62.48, 782.19) * mm, v(-9.54, 773.5) * mm, v(-15.8, 772.64) * mm]});
            skFitSpline(sketch, "E986", {"points": [v(239.88, 403.66) * mm, v(269.93, 462.93) * mm, v(289.63, 548.22) * mm, v(263.32, 640.4) * mm, v(250.14, 680.24) * mm, v(232.26, 718.58) * mm, v(213.3, 744.34) * mm, v(203, 758.68) * mm, v(199.58, 763.23) * mm]});
            skFitSpline(sketch, "E987", {"points": [v(165.34, 424.2) * mm, v(173.63, 423.37) * mm, v(199.24, 419.43) * mm, v(223.99, 411.17) * mm, v(239.88, 403.66) * mm]});
            skFitSpline(sketch, "E988", {"points": [v(-15.8, 772.64) * mm, v(-10.77, 770) * mm, v(3.25, 762.3) * mm, v(26, 747.84) * mm, v(50.39, 728.34) * mm, v(79.98, 701.56) * mm, v(116.45, 663.64) * mm, v(142.85, 616.01) * mm, v(156, 575.1) * mm, v(164.55, 535.07) * mm, v(170.6, 485.5) * mm, v(168.58, 443.87) * mm, v(165.34, 424.2) * mm]});
            skFitSpline(sketch, "E989", {"points": [v(-330, 637.94) * mm, v(-368.18, 607.97) * mm, v(-435.35, 542.78) * mm, v(-488.57, 465.52) * mm, v(-510.5, 426.6) * mm]});
            skFitSpline(sketch, "E990", {"points": [v(30.53, 398.56) * mm, v(26.6, 420.37) * mm, v(16.1, 458.73) * mm, v(-12.97, 513.78) * mm, v(-57.4, 563.03) * mm, v(-119.49, 605.37) * mm, v(-187.78, 627.36) * mm, v(-249.48, 638.02) * mm, v(-295, 637.86) * mm, v(-321.2, 638.44) * mm, v(-330, 637.94) * mm]});
            skFitSpline(sketch, "E991", {"points": [v(-48.6, 337.4) * mm, v(-34.02, 353.81) * mm, v(-8.72, 376.25) * mm, v(20.18, 393.35) * mm, v(30.53, 398.56) * mm]});
            skFitSpline(sketch, "E992", {"points": [v(-510.5, 426.6) * mm, v(-506.72, 428.48) * mm, v(-492.27, 435.53) * mm, v(-467.64, 447) * mm, v(-432.19, 460.73) * mm, v(-396.3, 469.2) * mm, v(-349.06, 477.42) * mm, v(-299.93, 480.16) * mm, v(-251.19, 476.5) * mm, v(-213.2, 469.33) * mm, v(-176.9, 455.1) * mm, v(-144.46, 436.87) * mm, v(-113.3, 415.94) * mm, v(-85.56, 388.92) * mm, v(-65.63, 365.9) * mm, v(-53.47, 347.17) * mm, v(-49.4, 339.06) * mm, v(-48.6, 337.4) * mm]});
            skFitSpline(sketch, "E993", {"points": [v(-608.84, 62.43) * mm, v(-608.87, 61.13) * mm, v(-610.6, -27.17) * mm, v(-595.76, -130.24) * mm, v(-563.66, -226.94) * mm, v(-558.8, -240.42) * mm]});
            skFitSpline(sketch, "E994", {"points": [v(-118.03, 184.73) * mm, v(-144.79, 219.17) * mm, v(-206.06, 252.33) * mm, v(-294.73, 267.34) * mm, v(-361.87, 262.2) * mm, v(-422.28, 235.55) * mm, v(-480.57, 204.84) * mm, v(-531, 159.1) * mm, v(-575.03, 113.52) * mm, v(-598.15, 79.26) * mm, v(-608.84, 62.43) * mm]});
            skFitSpline(sketch, "E995", {"points": [v(-114.62, 80.02) * mm, v(-119.65, 104.97) * mm, v(-122.5, 140.2) * mm, v(-119.35, 175.2) * mm, v(-118.04, 184.74) * mm]});
            skFitSpline(sketch, "E996", {"points": [v(-558.8, -240.42) * mm, v(-557.73, -236.29) * mm, v(-549.09, -204.3) * mm, v(-528.57, -145.35) * mm, v(-485.07, -68.59) * mm, v(-429.86, -0.77) * mm, v(-371.4, 47.27) * mm, v(-316.25, 73.86) * mm, v(-272.5, 87.38) * mm, v(-227.49, 93.38) * mm, v(-183.9, 93.65) * mm, v(-145.2, 90.66) * mm, v(-121.81, 83.2) * mm, v(-114.62, 80.02) * mm]});
            skFitSpline(sketch, "E997.0", {"points": [v(35.45, 399.45) * mm, v(33.66, 409.35) * mm, v(29.28, 429.09) * mm, v(21.52, 453.2) * mm, v(13.78, 471.96) * mm, v(7.17, 485.7) * mm, v(-0.22, 499.02) * mm, v(-8.4, 511.89) * mm, v(-17.37, 524.2) * mm, v(-27.05, 535.97) * mm, v(-37.37, 547.17) * mm, v(-48.28, 557.82) * mm, v(-59.7, 567.9) * mm, v(-71.6, 577.4) * mm, v(-83.97, 586.29) * mm, v(-96.77, 594.52) * mm, v(-107.79, 600.8) * mm, v(-116.79, 605.47) * mm, v(-125.9, 609.87) * mm, v(-137.51, 614.91) * mm, v(-151.7, 620.27) * mm, v(-166.11, 624.98) * mm, v(-178.26, 628.44) * mm, v(-188.03, 630.94) * mm, v(-197.84, 633.29) * mm, v(-210.16, 635.93) * mm, v(-222.57, 638.13) * mm, v(-232.55, 639.59) * mm, v(-240.05, 640.52) * mm, v(-247.57, 641.3) * mm, v(-255.12, 641.89) * mm, v(-262.65, 642.31) * mm, v(-270.17, 642.6) * mm, v(-277.68, 642.8) * mm, v(-285.18, 642.92) * mm, v(-292.66, 643) * mm, v(-298.88, 643.07) * mm, v(-303.84, 643.13) * mm, v(-308.82, 643.2) * mm, v(-315.08, 643.28) * mm, v(-322.66, 643.25) * mm, v(-327.74, 643.07) * mm, v(-330.3, 642.93) * mm]});
            skSolve(sketch);
        }
        {
            var Q0;
            Q0=makeQuery(id+"F0.imprint","IMPRINT",FACE,{"disambiguationData":[TD([[makeQuery(id+"F0.imprint","IMPRINT",EDGE,{"derivedFrom":sQuery(id+"F0.wireOp",EDGE,"E0")}),1.0]])]});
            extrude(context, id + "F1", {"entities" : qUnion([Q0]), "depth" : 127 * mm});
        }
    });
